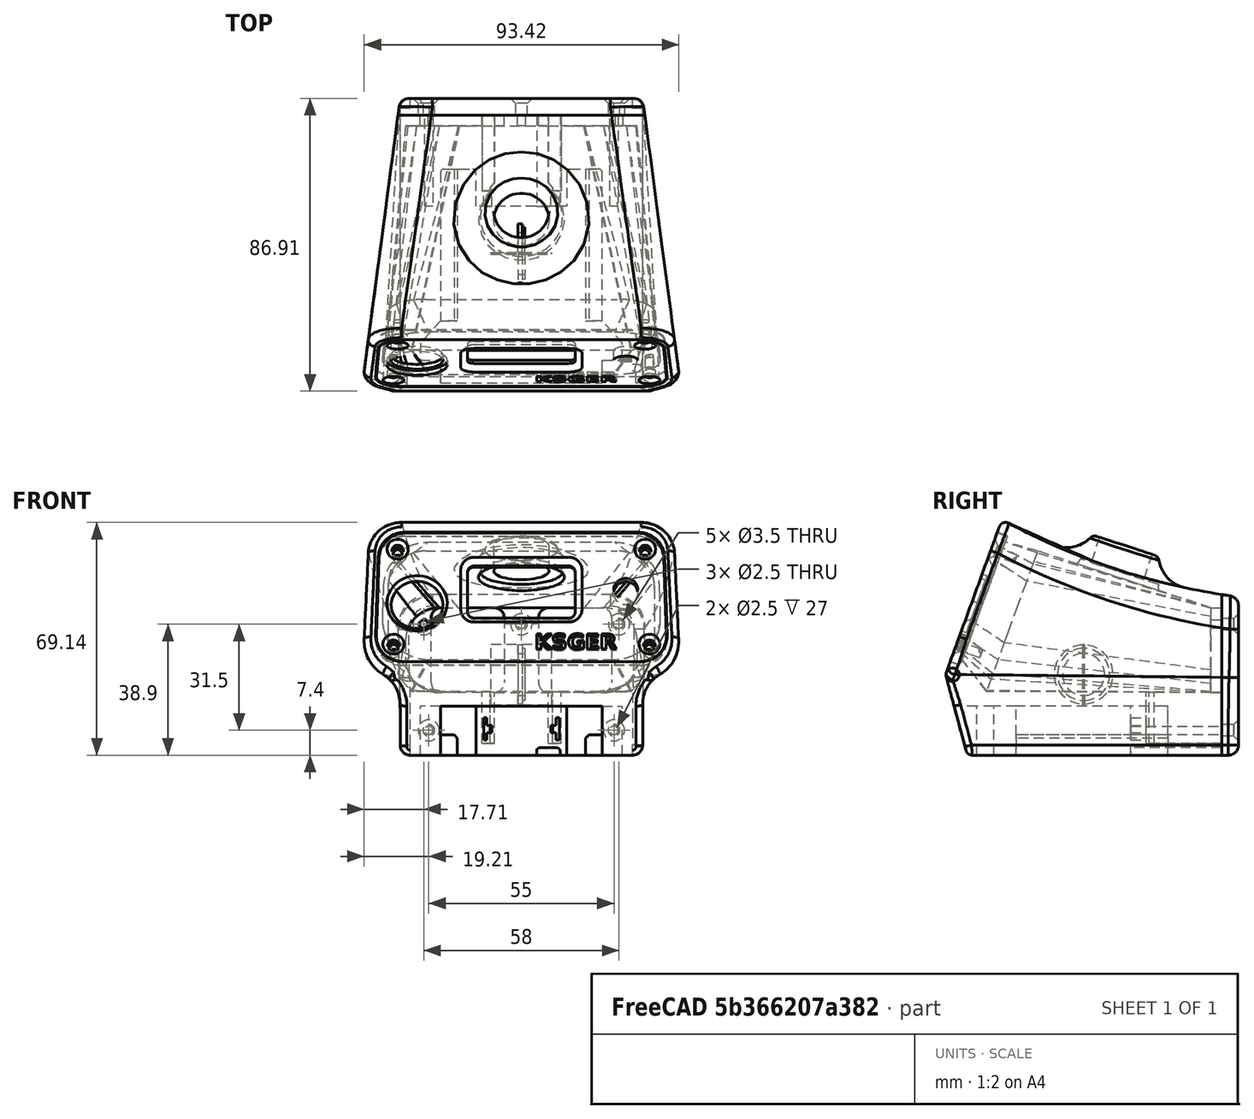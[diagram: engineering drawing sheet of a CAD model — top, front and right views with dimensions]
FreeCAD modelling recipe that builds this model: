
FCSTD DOCUMENT  (FreeCAD 0.20R29410 (Git))
Label: solder_station5c_snap
License: All rights reserved
LicenseURL: http://en.wikipedia.org/wiki/All_rights_reserved
objects: Sketcher::SketchObject×22, PartDesign::Pocket×12, PartDesign::Fillet×8, Part::FeaturePython×6, PartDesign::Body×5, Mesh::Feature×5, App::DocumentObjectGroup×4, PartDesign::FeatureBase×3, PartDesign::Chamfer×3, PartDesign::Pad×2, PartDesign::Revolution×2, Spreadsheet::Sheet×1, Part::Plane×1, Part::Loft×1, Part::Extrusion×1, Part::MultiCommon×1, Part::Box×1, PartDesign::SubtractiveLoft×1, PartDesign::Groove×1, PartDesign::Plane×1, +2 more types
note: 101 computed .brp shape members not serialized (recipe doc carries the construction recipe); baked Part::Feature solids carry a one-line shape summary decoded from their .brp

FEATURE [Sketcher::SketchObject] Sketch  label="RearSupport"
  AttachmentOffset = pos=(0,0,-37.8) rot=(0,0,1;0rad)
  FullyConstrained = true
  MapMode = 5
  Placement = pos=(0,37.8,8.4e-15) rot=(1,0,0;1.5708rad)
  Support = -> [XZ_Plane005]
  expr: .AttachmentOffset.Base.z = -<<param>>.mid_depth / 2 + <<param>>.wall
  expr: Constraints[24] = 3
  expr: Constraints[37] = <<param>>.bottom_height
  expr: Constraints[38] = <<param>>.floor
  expr: Constraints[39] = <<param>>.rear_height - <<param>>.wall
  expr: Constraints[47] = <<param>>.reart_screw_width2
  expr: Constraints[48] = <<param>>.rear_screw_width1
  expr: Constraints[49] = <<param>>.screw_hole
  expr: Constraints[50] = <<param>>.rear_screw_height
  expr: Constraints[51] = <<param>>.rear_screw_height
  expr: Constraints[52] = <<param>>.rear_screw_offset
  sketch-geometry (22):
    g0: LineSegment StartX=-23.8 StartY=19.8 StartZ=0 EndX=-8.1 EndY=19.8 EndZ=0
    g1: LineSegment StartX=26.8 StartY=16.8 StartZ=0 EndX=26.8 EndY=-2.4 EndZ=0
    g2: LineSegment StartX=23.8 StartY=-5.4 StartZ=0 EndX=8.1 EndY=-5.4 EndZ=0
    g3: LineSegment StartX=-26.8 StartY=-2.4 StartZ=0 EndX=-26.8 EndY=16.8 EndZ=0
    g4: LineSegment StartX=-5.1 StartY=16.8 StartZ=0 EndX=-5.1 EndY=-2.4 EndZ=0
    g5: LineSegment StartX=5.1 StartY=16.8 StartZ=0 EndX=5.1 EndY=-2.4 EndZ=0
    g6: LineSegment StartX=8.1 StartY=19.8 StartZ=0 EndX=23.8 EndY=19.8 EndZ=0
    g7: LineSegment StartX=-8.1 StartY=-5.4 StartZ=0 EndX=-23.8 EndY=-5.4 EndZ=0
    g8: ArcOfCircle CenterX=-8.1 CenterY=16.8 CenterZ=0 NormalX=0 NormalY=0 NormalZ=1 AngleXU=0 Radius=3 StartAngle=0 EndAngle=1.5708
    g9: ArcOfCircle CenterX=8.1 CenterY=16.8 CenterZ=0 NormalX=0 NormalY=0 NormalZ=1 AngleXU=0 Radius=3 StartAngle=1.5708 EndAngle=3.14159
    g10: ArcOfCircle CenterX=-8.1 CenterY=-2.4 CenterZ=0 NormalX=0 NormalY=0 NormalZ=1 AngleXU=0 Radius=3 StartAngle=4.71239 EndAngle=6.28319
    g11: ArcOfCircle CenterX=8.1 CenterY=-2.4 CenterZ=0 NormalX=0 NormalY=0 NormalZ=1 AngleXU=0 Radius=3 StartAngle=3.14159 EndAngle=4.71239
    g12: ArcOfCircle CenterX=-23.8 CenterY=16.8 CenterZ=0 NormalX=0 NormalY=0 NormalZ=1 AngleXU=0 Radius=3 StartAngle=1.5708 EndAngle=3.14159
    g13: ArcOfCircle CenterX=-23.8 CenterY=-2.4 CenterZ=0 NormalX=0 NormalY=0 NormalZ=1 AngleXU=0 Radius=3 StartAngle=3.14159 EndAngle=4.71239
    g14: ArcOfCircle CenterX=23.8 CenterY=16.8 CenterZ=0 NormalX=0 NormalY=0 NormalZ=1 AngleXU=0 Radius=3 StartAngle=3e-16 EndAngle=1.5708
    g15: ArcOfCircle CenterX=23.8 CenterY=-2.4 CenterZ=0 NormalX=0 NormalY=0 NormalZ=1 AngleXU=0 Radius=3 StartAngle=4.71239 EndAngle=6.28319
    g16: Circle CenterX=0 CenterY=-24 CenterZ=0 NormalX=0 NormalY=0 NormalZ=1 AngleXU=0 Radius=3
    g17: Circle CenterX=0 CenterY=14.9 CenterZ=0 NormalX=0 NormalY=0 NormalZ=1 AngleXU=0 Radius=1.25
    g18: Circle CenterX=-29 CenterY=14.9 CenterZ=0 NormalX=0 NormalY=0 NormalZ=1 AngleXU=0 Radius=1.25
    g19: Circle CenterX=-27.5 CenterY=-16.6 CenterZ=0 NormalX=0 NormalY=0 NormalZ=1 AngleXU=0 Radius=1.25
    g20: Circle CenterX=27.5 CenterY=-16.6 CenterZ=0 NormalX=0 NormalY=0 NormalZ=1 AngleXU=0 Radius=1.25
    g21: Circle CenterX=29 CenterY=14.9 CenterZ=0 NormalX=0 NormalY=0 NormalZ=1 AngleXU=0 Radius=1.25
  constraints (53):
    c: Horizontal(g0)
    c: Horizontal(g2)
    c: Vertical(g1)
    c: Vertical(g3)
    c: Vertical(g4)
    c: Vertical(g5)
    c: Tangent(g0,g6)
    c: Tangent(g2,g7)
    c: Tangent(g0,g8) = 1.5708
    c: Tangent(g4,g8) = 1.5708
    c: Tangent(g5,g9) = -1.5708
    c: Tangent(g6,g9) = 1.5708
    c: Tangent(g7,g10) = 1.5708
    c: Tangent(g4,g10) = 1.5708
    c: Tangent(g5,g11) = -1.5708
    c: Tangent(g2,g11) = 1.5708
    c: Tangent(g0,g12) = 1.5708
    c: Tangent(g3,g12) = 1.5708
    c: Tangent(g3,g13) = 1.5708
    c: Tangent(g7,g13) = 1.5708
    c: Tangent(g6,g14) = 1.5708
    c: Tangent(g1,g14) = 1.5708
    c: Tangent(g1,g15) = 1.5708
    c: Tangent(g2,g15) = 1.5708
    c: Radius(g9) = 3
    c: Equal(g12,g13)
    c: Equal(g13,g10)
    c: Equal(g10,g8)
    c: Equal(g11,g15)
    c: Equal(g15,g14)
    c: Equal(g14,g9)
    c: DistanceX(g4,g-1) = 5.1
    c: DistanceX(g5,g1) = 21.7
    c: Symmetric(g4,g5,g-2)
    c: Equal(g7,g2)
    c: PointOnObject(g16,g-2)
    c: Radius(g16) = 3
    c: DistanceY(g16,g-1) = 24
    c: DistanceY(g16,g2) = 18.6
    c: DistanceY(g16,g6) = 43.8
    c: PointOnObject(g17,g-2)
    c: Equal(g21,g18)
    c: Equal(g18,g19)
    c: Equal(g19,g20)
    c: Equal(g18,g17)
    c: Symmetric(g20,g19,g-2)
    c: Symmetric(g18,g21,g-2)
    c: DistanceX(g19,g20) = 55
    c: DistanceX(g18,g21) = 58
    c: Diameter(g19) = 2.5
    c: DistanceY(g20,g21) = 31.5
    c: DistanceY(g20,g17) = 31.5
    c: DistanceY(g16,g19) = 7.4
FEATURE [Spreadsheet::Sheet] Spreadsheet  label="param"
  cells = A1=Body; B2=top_depth; C2(top_depth)=70; B3=mid_depth; C3(mid_depth)=82; D3=half is rear reference; B4=bottom_depth; C4(bottom_depth)=75; B6=bottom_width; C6(bottom_width)=72; B7=bottom_height; C7(bottom_height)=24; B8=bottom_angle; C8(bottom_angle)=15; B10=rear_width; C10(rear_width)=72; B11=rear_height; C11(rear_height)=47; F11=41; B13=mid_width; C13(mid_width)=80; B14=mid_height; C14(mid_height)=56; F14=50; B16=front_width1; C16(front_width1)=92; D16=@top; E16=upper; F16=91; B17=front_width2; C17(front_width2)=95; D17=@mid; E17=lower; F17=94; B18=front_height; C18(front_height)=70; F18=64; B19=front_angle; C19(front_angle)=20; B21=wall; C21(wall)=3.2; B22=radius_big; C22(radius_big)=10; B23=radius_medium; C23(radius_medium)=3; B24=radius_small; C24(radius_small)=2; B25=arch; C25(arch)=200; A27=Button; B28=button_offset; C28(button_offset)=10; B29=button_inside_dia; C29(button_inside_dia)=20; B30=button_outside_dia; C30(button_outside_dia)=22; B31=button_height; C31(button_height)=30.6; F31=26; B32=button_extension; C32(button_extension)=8; B33=button_fillet; C33(button_fillet)=12; B34=button_angle; C34(button_angle)=-18; F34=-17; B35=button_hole; C35(button_hole)=16.4; B36=button_hole_center; C36(button_hole_center)=-0.5; A38=Battery Cuts; B39=batt_carveout; C39(batt_carveout)=14.6; B40=batt_rail; C40(batt_rail)=6; B41=batt_rail_length; C41(batt_rail_length)=45; A43=Terminals; B44=terminal_height; C44(terminal_height)=6.6; B45=terminal_thickness; C45(terminal_thickness)=1; B46=terminal_seperation; C46(terminal_seperation)=21.5; B47=terminal_offset; C47(terminal_offset)=4.5; B48=terminal_depth; C48(terminal_depth)=22.5; A50=Box Interior; B51=floor; C51(floor)=18.6; B52=rear_inside_width; C52(rear_inside_width)==C10 - C21; D52=calc; B53=rear_inside_height; C53(rear_inside_height)==C11 - C21; D53=calc; B54=mid_inside_width; C54(mid_inside_width)==C13; D54=calc; B55=mid_inside_height; C55(mid_inside_height)==C14 + 7; D55=calc; F55=6; B56=front_inside_width1; C56(front_inside_width1)==C63 - C59 * 2; D56=calc; E56=upper; B57=front_inside_width2; C57(front_inside_width2)==C64 - C59 * 2; D57=calc; E57=lower; B58=front_inside_height; C58(front_inside_height)==C65 - C60 * 2; D58=calc; B59=front_width_lip_width; C59(front_width_lip_width)=3; B60=front_inside_lip_height; C60(front_inside_lip_height)=2; A62=Face; B63=face_width1; C63(face_width1)==84 + 1; D63=Dimension of opening in case (upper); B64=face_width2; C64(face_width2)==85.5 + 1; D64=Dimension of opening in case (lower); B65=face_height; C65(face_height)=41; D65=Dimension of actual opening in case; F65=35; B66=face_fit; C66(face_fit)=0.4; D66=Reduction of face dimensions for clearance with case; B67=face_thickness; C67(face_thickness)=3; D67=Face thickness; B68=face_radius; C68(face_radius)=8; D68=Corner radius; B69=face_offset; C69(face_offset)=2.8; D69=Axis origin to bottom face (reference); F69=2.8; B70=face_knob_x; C70(face_knob_x)=31; D70=Vertical center line of face to center of knob; B71=face_knob_y; C71(face_knob_y)=22.7; D71=Bottom of face to center of knob; B72=face_knob_tab; C72(face_knob_tab)=n/a; D72=Center to center distance of rotary dial shaft to tab; B73=face_knob_hole; C73(face_knob_hole)=7.2; D73=Hole size fo shaft; B74=face_screen_x; C74(face_screen_x)=15; D74=Center of knob to right edge of screen; B75=face_screen_y; C75(face_screen_y)=n/a; D75=Bottom of face to center of screen; B76=face_screen_width; C76(face_screen_width)=32; D76=Width of screen opening; B77=face_screen_height; C77(face_screen_height)=16.5; D77=Height of screen opening; B78=face_screen_radius; C78(face_screen_radius)=2; D78=Radius of screen opening; B79=face_plug_x; C79(face_plug_x)=31; D79=Center line of face to center of plug; B80=face_plug_y; C80(face_plug_y)=18.7; D80=Bottom of face to center of plug; B81=face_plug_hole; C81(face_plug_hole)=15.5; D81=Hole size for plug body; A83=Screws; B84=screw_hole; C84(screw_hole)=2.5; B86=front_screw_width1; C86(front_screw_width1)=73.5; D86=upper; B87=front_screw_width2; C87(front_screw_width2)=76; D87=lower; B88=front_screw_height; C88(front_screw_height)=30; F88=24; B89=front_screw_offset; C89(front_screw_offset)=5.5; B91=rear_screw_width1; C91(rear_screw_width1)=58; B92=reart_screw_width2; C92(reart_screw_width2)=55; B93=rear_screw_height; C93(rear_screw_height)=31.5; F93=25.5; +5 more cells
FEATURE [Sketcher::SketchObject] Sketch008  label="SketchButtonHole"
  AttachmentOffset = pos=(0,-0.5,30.6) rot=(1,0,0;-0.314159rad)
  FullyConstrained = true
  MapMode = 5
  Placement = pos=(0,-0.5,30.6) rot=(1,0,0;5.96903rad)
  Support = -> [XY_Plane005]
  expr: .AttachmentOffset.Base.y = <<param>>.button_hole_center
  expr: .AttachmentOffset.Base.z = <<param>>.button_height
  expr: .AttachmentOffset.Rotation.Angle = <<param>>.button_angle
  expr: Constraints[0] = <<param>>.button_hole
  expr: Constraints[2] = <<param>>.button_offset
  sketch-geometry (1):
    g0: Circle CenterX=0 CenterY=10 CenterZ=0 NormalX=0 NormalY=0 NormalZ=1 AngleXU=0 Radius=8.2
  constraints (3):
    c: Diameter(g0) = 16.4
    c: PointOnObject(g0,g-2)
    c: DistanceY(g-1,g0) = 10
FEATURE [Sketcher::SketchObject] Sketch012  label="SketchSide"
  AttachmentOffset = pos=(2.5,0,0) rot=(0,0,1;0rad)
  FullyConstrained = true
  MapMode = 5
  Placement = pos=(6e-16,2.5,-6e-16) rot=(0.57735,0.57735,0.57735;2.0944rad)
  Support = -> [YZ_Plane006]
  expr: .AttachmentOffset.Base.x = <<param>>.back_thickness / 2
  expr: Constraints[10] = <<param>>.bottom_height
  expr: Constraints[11] = 90 - <<param>>.bottom_angle
  expr: Constraints[12] = 90 - <<param>>.front_angle
  expr: Constraints[16] = <<param>>.front_height
  expr: Constraints[4] = <<param>>.rear_height - <<param>>.bottom_height
  expr: Constraints[5] = <<param>>.arch
  expr: Constraints[6] = <<param>>.mid_depth + <<param>>.back_thickness
  sketch-geometry (6):
    g0: LineSegment StartX=43.5 StartY=0 StartZ=0 EndX=43.5 EndY=23 EndZ=0
    g1: LineSegment StartX=-43.5 StartY=0 StartZ=0 EndX=-26.7574 EndY=46 EndZ=0
    g2: ArcOfCircle CenterX=69.5235 CenterY=221.3 CenterZ=0 NormalX=0 NormalY=0 NormalZ=1 AngleXU=0 Radius=200 StartAngle=4.21013 EndAngle=4.5819
    g3: LineSegment StartX=-43.5 StartY=0 StartZ=0 EndX=-37.0692 EndY=-24 EndZ=0
    g4: LineSegment StartX=-37.0692 StartY=-24 StartZ=0 EndX=43.5 EndY=-24 EndZ=0
    g5: LineSegment StartX=43.5 StartY=-24 StartZ=0 EndX=43.5 EndY=0 EndZ=0
  constraints (18):
    c: PointOnObject(g1,g-1)
    c: Vertical(g0)
    c: Coincident(g2,g0)
    c: Symmetric(g1,g0,g-2)
    c: DistanceY(g0,g0) = 23
    c: Radius(g2) = 200
    c: DistanceX(g1,g0) = 87
    c: Horizontal(g4)
    c: Coincident(g5,g4)
    c: Vertical(g5)
    c: DistanceY(g4,g-1) = 24
    c: Angle(g3,g-1) = 1.309
    c: Angle(g-1,g1) = 1.22173
    c: Coincident(g3,g1)
    c: Coincident(g5,g0)
    c: Coincident(g2,g1)
    c: DistanceY(g4,g1) = 70
    c: Coincident(g3,g4)
FEATURE [Sketcher::SketchObject] Sketch018  label="SketchBat1"
  AttachmentOffset = pos=(0,0,-24) rot=(0,0,1;0rad)
  FullyConstrained = true
  MapMode = 5
  Placement = pos=(0,0,-24) rot=(0,0,1;0rad)
  Support = -> [XY_Plane005]
  expr: .AttachmentOffset.Base.z = -<<param>>.bottom_height
  expr: Constraints[63] = <<param>>.batt_rail_length
  expr: Constraints[64] = <<param>>.mid_depth / 2
  sketch-geometry (21):
    g0: LineSegment StartX=-24 StartY=-41.7082 StartZ=0 EndX=24 EndY=-41.7082 EndZ=0
    g1: LineSegment StartX=24 StartY=-41.7082 StartZ=0 EndX=24 EndY=-31.7082 EndZ=0
    g2: LineSegment StartX=24 StartY=-31.7082 StartZ=0 EndX=30 EndY=-31.7082 EndZ=0
    g3: LineSegment StartX=30 StartY=-31.7082 StartZ=0 EndX=30 EndY=-26.7082 EndZ=0
    g4: LineSegment StartX=30 StartY=-26.7082 StartZ=0 EndX=24 EndY=-20 EndZ=0
    g5: LineSegment StartX=24 StartY=-20 StartZ=0 EndX=24 EndY=24 EndZ=0
    g6: LineSegment StartX=13.5 StartY=24 StartZ=0 EndX=13.5 EndY=14 EndZ=0
    g7: LineSegment StartX=13.5 StartY=14 StartZ=0 EndX=-13.5 EndY=14 EndZ=0
    g8: LineSegment StartX=-13.5 StartY=14 StartZ=0 EndX=-13.5 EndY=24 EndZ=0
    g9: LineSegment StartX=-24 StartY=24 StartZ=0 EndX=-24 EndY=-20 EndZ=0
    g10: LineSegment StartX=-24 StartY=-20 StartZ=0 EndX=-30 EndY=-26.7082 EndZ=0
    g11: LineSegment StartX=-30 StartY=-26.7082 StartZ=0 EndX=-30 EndY=-31.7082 EndZ=0
    g12: LineSegment StartX=-30 StartY=-31.7082 StartZ=0 EndX=-24 EndY=-31.7082 EndZ=0
    g13: LineSegment StartX=-24 StartY=-31.7082 StartZ=0 EndX=-24 EndY=-41.7082 EndZ=0
    g14: Circle CenterX=0 CenterY=41 CenterZ=0 NormalX=0 NormalY=0 NormalZ=1 AngleXU=0 Radius=4
    g15: ArcOfCircle CenterX=-14.5 CenterY=24 CenterZ=0 NormalX=0 NormalY=0 NormalZ=1 AngleXU=0 Radius=1 StartAngle=6.28318 EndAngle=7.85399
    g16: LineSegment StartX=-23 StartY=25 StartZ=0 EndX=-14.5 EndY=25 EndZ=0
    g17: LineSegment StartX=14.5 StartY=25 StartZ=0 EndX=23 EndY=25 EndZ=0
    g18: ArcOfCircle CenterX=-23 CenterY=24 CenterZ=0 NormalX=0 NormalY=0 NormalZ=1 AngleXU=0 Radius=1 StartAngle=1.57079 EndAngle=3.1416
    g19: ArcOfCircle CenterX=14.5 CenterY=24 CenterZ=0 NormalX=0 NormalY=0 NormalZ=1 AngleXU=0 Radius=1 StartAngle=1.5708 EndAngle=3.14159
    g20: ArcOfCircle CenterX=23 CenterY=24 CenterZ=0 NormalX=0 NormalY=0 NormalZ=1 AngleXU=0 Radius=1.00001 StartAngle=2.75124e-06 EndAngle=1.5708
  constraints (65):
    c: Horizontal(g0)
    c: Coincident(g1,g0)
    c: Vertical(g1)
    c: Coincident(g2,g1)
    c: Horizontal(g2)
    c: Coincident(g3,g2)
    c: Coincident(g3,g4)
    c: Vertical(g5)
    c: Coincident(g6,g7)
    c: Coincident(g7,g8)
    c: Vertical(g8)
    c: Vertical(g9)
    c: Coincident(g10,g11)
    c: Vertical(g11)
    c: Coincident(g11,g12)
    c: Horizontal(g12)
    c: Coincident(g12,g13)
    c: Equal(g6,g8)
    c: Equal(g5,g9)
    c: Equal(g4,g10)
    c: Equal(g3,g11)
    c: Equal(g12,g2)
    c: Equal(g1,g13)
    c: Coincident(g13,g0)
    c: Vertical(g13)
    c: DistanceX(g7,g7) = 27
    c: Symmetric(g7,g6,g-2)
    c: Distance(g4) = 9
    c: Vertical(g3)
    c: DistanceY(g3,g3) = 5
    c: DistanceX(g2,g2) = 6
    c: DistanceY(g1,g1) = 10
    c: DistanceX(g0,g0) = 48
    c: PointOnObject(g14,g-2)
    c: Coincident(g9,g10)
    c: Coincident(g5,g4)
    c: Coincident(g15,g8)
    c: Coincident(g16,g15)
    c: Tangent(g15,g8)
    c: Horizontal(g16)
    c: Horizontal(g17)
    c: DistanceX(g9,g5) = 48
    c: Symmetric(g4,g9,g-2)
    c: Equal(g16,g17)
    c: Coincident(g18,g9)
    c: Coincident(g18,g16)
    c: Equal(g18,g15)
    c: Tangent(g18,g16)
    c: Tangent(g18,g9)
    c: DistanceY(g6,g17) = 11
    c: Vertical(g6)
    c: Coincident(g19,g6)
    c: Coincident(g19,g17)
    c: Coincident(g20,g17)
    c: Coincident(g20,g5)
    c: Tangent(g20,g17)
    c: Tangent(g20,g5)
    c: Tangent(g19,g6)
    c: Tangent(g19,g17)
    c: Equal(g15,g19)
    c: Radius(g19) = 1
    c: Radius(g14) = 4
    c: DistanceY(g15,g14) = 16
    c: DistanceY(g9,g16) = 45
    c: DistanceY(g-1,g14) = 41
FEATURE [Sketcher::SketchObject] Sketch019  label="SketchBat2"
  AttachmentOffset = pos=(0,0,-25) rot=(0,0,1;0rad)
  FullyConstrained = true
  MapMode = 5
  Placement = pos=(0,25,5.6e-15) rot=(1,0,0;1.5708rad)
  Support = -> [XZ_Plane005]
  expr: .AttachmentOffset.Base.z = -<<param>>.mid_depth / 2 + 16
  expr: Constraints[17] = <<param>>.bottom_height
  expr: Constraints[18] = <<param>>.batt_rail
  expr: Constraints[19] = 48.01mm
  sketch-geometry (10):
    g0: LineSegment StartX=-24.005 StartY=-18 StartZ=0 EndX=-20.005 EndY=-18 EndZ=0
    g1: LineSegment StartX=-19.005 StartY=-24 StartZ=0 EndX=-24.005 EndY=-24 EndZ=0
    g2: LineSegment StartX=-24.005 StartY=-24 StartZ=0 EndX=-24.005 EndY=-18 EndZ=0
    g3: LineSegment StartX=24.005 StartY=-18 StartZ=0 EndX=20.005 EndY=-18 EndZ=0
    g4: LineSegment StartX=19.005 StartY=-24 StartZ=0 EndX=24.005 EndY=-24 EndZ=0
    g5: LineSegment StartX=24.005 StartY=-24 StartZ=0 EndX=24.005 EndY=-18 EndZ=0
    g6: LineSegment StartX=-19.005 StartY=-19 StartZ=0 EndX=-19.005 EndY=-24 EndZ=0
    g7: LineSegment StartX=19.005 StartY=-24 StartZ=0 EndX=19.005 EndY=-19 EndZ=0
    g8: LineSegment StartX=-20.005 StartY=-18 StartZ=0 EndX=-19.005 EndY=-19 EndZ=0
    g9: LineSegment StartX=19.005 StartY=-19 StartZ=0 EndX=20.005 EndY=-18 EndZ=0
  constraints (29):
    c: Coincident(g1,g2)
    c: Coincident(g2,g0)
    c: Horizontal(g0)
    c: Horizontal(g1)
    c: Vertical(g2)
    c: Coincident(g4,g5)
    c: Coincident(g5,g3)
    c: Horizontal(g3)
    c: Horizontal(g4)
    c: Vertical(g5)
    c: Coincident(g6,g1)
    c: Vertical(g6)
    c: Equal(g1,g4)
    c: Coincident(g7,g4)
    c: Vertical(g7)
    c: Equal(g6,g7)
    c: Symmetric(g1,g4,g-2)
    c: DistanceY(g1,g-1) = 24
    c: DistanceY(g4,g3) = 6
    c: DistanceX(g1,g4) = 48.01
    c: DistanceX(g4,g4) = 5
    c: Coincident(g8,g0)
    c: Coincident(g8,g6)
    c: Coincident(g9,g7)
    c: Coincident(g9,g3)
    c: Equal(g0,g3)
    c: Equal(g2,g5)
    c: DistanceX(g0,g0) = 4
    c: DistanceY(g1,g6) = 5
FEATURE [Sketcher::SketchObject] Sketch021  label="SketchButton"
  AttachmentOffset = pos=(10,30.6,0) rot=(0,0,1;-0.314159rad)
  FullyConstrained = true
  MapMode = 5
  Placement = pos=(-4.6e-15,10,30.6) rot=(-0.506732,-0.697457,-0.506732;4.35963rad)
  Support = -> [YZ_Plane005]
  expr: .AttachmentOffset.Base.x = <<param>>.button_offset
  expr: .AttachmentOffset.Base.y = <<param>>.button_height
  expr: .AttachmentOffset.Rotation.Angle = <<param>>.button_angle
  expr: Constraints[6] = <<param>>.button_extension
  expr: Constraints[7] = <<param>>.button_outside_dia / 2
  sketch-geometry (5):
    g0: LineSegment StartX=0 StartY=0 StartZ=0 EndX=0 EndY=8 EndZ=0
    g1: LineSegment StartX=0 StartY=8 StartZ=0 EndX=9 EndY=8 EndZ=0
    g2: LineSegment StartX=0 StartY=0 StartZ=0 EndX=11 EndY=0 EndZ=0
    g3: LineSegment StartX=11 StartY=0 StartZ=0 EndX=11 EndY=6 EndZ=0
    g4: ArcOfCircle CenterX=9 CenterY=6 CenterZ=0 NormalX=0 NormalY=0 NormalZ=1 AngleXU=0 Radius=2 StartAngle=1e-16 EndAngle=1.5708
  constraints (13):
    c: Coincident(g0,g-1)
    c: PointOnObject(g0,g-2)
    c: Coincident(g1,g0)
    c: Horizontal(g1)
    c: Coincident(g2,g0)
    c: Horizontal(g2)
    c: DistanceY(g0,g0) = 8
    c: DistanceX(g2,g2) = 11
    c: Coincident(g3,g2)
    c: Vertical(g3)
    c: Radius(g4) = 2
    c: Tangent(g4,g1) = 1.5708
    c: Tangent(g4,g3) = -1.5708
FEATURE [Sketcher::SketchObject] Sketch022  label="SketchRearInside"
  AttachmentOffset = pos=(0,0,-37.8) rot=(0,0,1;0rad)
  FullyConstrained = true
  MapMode = 5
  Placement = pos=(0,37.8,8.4e-15) rot=(1,0,0;1.5708rad)
  Support = -> [XZ_Plane005]
  expr: .AttachmentOffset.Base.z = -<<param>>.mid_depth / 2 + <<param>>.wall
  expr: Constraints[12] = <<param>>.radius_big
  expr: Constraints[18] = <<param>>.rear_inside_width
  expr: Constraints[26] = <<param>>.bottom_height
  expr: Constraints[27] = <<param>>.rear_inside_height
  expr: Constraints[29] = <<param>>.floor
  sketch-geometry (9):
    g0: LineSegment StartX=-34.4 StartY=9.80002 StartZ=0 EndX=-34.4 EndY=4.59998 EndZ=0
    g1: LineSegment StartX=-24.4 StartY=-5.4 StartZ=0 EndX=24.4 EndY=-5.4 EndZ=0
    g2: LineSegment StartX=34.4 StartY=4.59998 StartZ=0 EndX=34.4 EndY=9.80002 EndZ=0
    g3: LineSegment StartX=-24.4 StartY=19.8 StartZ=0 EndX=24.4 EndY=19.8 EndZ=0
    g4: ArcOfCircle CenterX=24.4 CenterY=9.8 CenterZ=0 NormalX=0 NormalY=0 NormalZ=1 AngleXU=0 Radius=10 StartAngle=1.745e-06 EndAngle=1.57079
    g5: ArcOfCircle CenterX=24.4 CenterY=4.6 CenterZ=0 NormalX=0 NormalY=0 NormalZ=1 AngleXU=0 Radius=10 StartAngle=4.71239 EndAngle=6.28318
    g6: ArcOfCircle CenterX=-24.4 CenterY=9.8 CenterZ=0 NormalX=0 NormalY=0 NormalZ=1 AngleXU=0 Radius=10 StartAngle=1.5708 EndAngle=3.14159
    g7: ArcOfCircle CenterX=-24.4 CenterY=4.6 CenterZ=0 NormalX=0 NormalY=0 NormalZ=1 AngleXU=0 Radius=10 StartAngle=3.14159 EndAngle=4.71239
    g8: Circle CenterX=0 CenterY=-24 CenterZ=0 NormalX=0 NormalY=0 NormalZ=1 AngleXU=0 Radius=3
  constraints (30):
    c: Vertical(g0)
    c: Horizontal(g1)
    c: Vertical(g2)
    c: Horizontal(g3)
    c: Equal(g3,g1)
    c: Equal(g0,g2)
    c: Coincident(g4,g3)
    c: Coincident(g4,g2)
    c: Coincident(g5,g2)
    c: Coincident(g5,g1)
    c: Coincident(g6,g0)
    c: Coincident(g6,g3)
    c: Radius(g6) = 10
    c: Equal(g6,g4)
    c: Equal(g4,g5)
    c: Coincident(g7,g1)
    c: Coincident(g7,g0)
    c: Equal(g5,g7)
    c: DistanceX(g0,g2) = 68.8
    c: Symmetric(g0,g2,g-2)
    c: Tangent(g4,g2)
    c: Tangent(g4,g3)
    c: Tangent(g5,g2)
    c: Tangent(g5,g1)
    c: Tangent(g6,g3)
    c: PointOnObject(g8,g-2)
    c: DistanceY(g8,g-1) = 24
    c: DistanceY(g8,g3) = 43.8
    c: Radius(g8) = 3
    c: DistanceY(g8,g1) = 18.6
FEATURE [Sketcher::SketchObject] Sketch024  label="SketchFaceCut"
  AttachmentOffset = pos=(0,0,37.6) rot=(1,0,0;-0.349066rad)
  FullyConstrained = true
  MapMode = 5
  Placement = pos=(0,-37.6,-8.3e-15) rot=(-1,0,0;5.06145rad)
  Support = -> [XZ_Plane005]
  expr: .AttachmentOffset.Base.z = <<param>>.mid_depth / 2 - <<param>>.face_thickness - 0.4
  expr: .AttachmentOffset.Rotation.Angle = -<<param>>.front_angle
  expr: Constraints[13] = <<param>>.face_radius
  expr: Constraints[22] = <<param>>.face_width1
  expr: Constraints[23] = <<param>>.face_width2
  expr: Constraints[24] = <<param>>.face_offset
  expr: Constraints[25] = <<param>>.face_height
  sketch-geometry (8):
    g0: LineSegment StartX=-34.5036 StartY=43.8 StartZ=0 EndX=34.5036 EndY=43.8 EndZ=0
    g1: LineSegment StartX=42.5 StartY=36.0399 StartZ=0 EndX=43.25 EndY=11.0399 EndZ=0
    g2: LineSegment StartX=35.2536 StartY=2.8 StartZ=0 EndX=-35.2536 EndY=2.8 EndZ=0
    g3: LineSegment StartX=-43.25 StartY=11.0399 StartZ=0 EndX=-42.5 EndY=36.0399 EndZ=0
    g4: ArcOfCircle CenterX=34.5036 CenterY=35.8 CenterZ=0 NormalX=0 NormalY=0 NormalZ=1 AngleXU=0 Radius=8 StartAngle=0.0299892 EndAngle=1.5708
    g5: ArcOfCircle CenterX=35.2536 CenterY=10.8 CenterZ=0 NormalX=0 NormalY=0 NormalZ=1 AngleXU=0 Radius=8 StartAngle=4.71239 EndAngle=6.31318
    g6: ArcOfCircle CenterX=-34.5036 CenterY=35.8 CenterZ=0 NormalX=0 NormalY=0 NormalZ=1 AngleXU=0 Radius=8 StartAngle=1.5708 EndAngle=3.1116
    g7: ArcOfCircle CenterX=-35.2536 CenterY=10.8 CenterZ=0 NormalX=0 NormalY=0 NormalZ=1 AngleXU=0 Radius=8 StartAngle=3.1116 EndAngle=4.71239
  constraints (27):
    c: Horizontal(g0)
    c: Coincident(g4,g0)
    c: Coincident(g4,g1)
    c: Coincident(g5,g1)
    c: Coincident(g5,g2)
    c: Coincident(g6,g0)
    c: Coincident(g6,g3)
    c: Coincident(g7,g3)
    c: Coincident(g7,g2)
    c: Equal(g1,g3)
    c: Equal(g4,g6)
    c: Equal(g6,g7)
    c: Equal(g7,g5)
    c: Radius(g4) = 8
    c: Tangent(g6,g3)
    c: Tangent(g7,g3)
    c: Tangent(g7,g2)
    c: Tangent(g6,g0)
    c: Tangent(g4,g0)
    c: Tangent(g4,g1)
    c: Tangent(g5,g1)
    c: Tangent(g5,g2)
    c: DistanceX(g3,g1) = 85
    c: DistanceX(g3,g1) = 86.5
    c: DistanceY(g-1,g2) = 2.8
    c: DistanceY(g2,g0) = 41
    c: Symmetric(g2,g2,g-2)
FEATURE [Sketcher::SketchObject] Sketch025  label="SketchMidInside"
  AttachmentOffset = pos=(0,0,27) rot=(1,0,0;-0.349066rad)
  FullyConstrained = true
  MapMode = 5
  Placement = pos=(0,-27,-6e-15) rot=(-1,0,0;5.06145rad)
  Support = -> [XZ_Plane005]
  expr: .AttachmentOffset.Base.z = <<param>>.mid_depth / 2 - 14
  expr: .AttachmentOffset.Rotation.Angle = -<<param>>.front_angle
  expr: Constraints[10] = <<param>>.radius_big + 1
  expr: Constraints[11] = <<param>>.floor
  expr: Constraints[12] = Spreadsheet.mid_inside_width - 1
  expr: Constraints[14] = <<param>>.mid_inside_height
  expr: Constraints[23] = <<param>>.mid_width - 15
  expr: Constraints[4] = <<param>>.bottom_height
  sketch-geometry (9):
    g0: LineSegment StartX=-28.5 StartY=39 StartZ=0 EndX=28.5 EndY=39 EndZ=0
    g1: LineSegment StartX=39.5 StartY=28 StartZ=0 EndX=39.5 EndY=10 EndZ=0
    g2: LineSegment StartX=32.5 StartY=-5.4 StartZ=0 EndX=-32.5 EndY=-5.4 EndZ=0
    g3: LineSegment StartX=-39.5 StartY=10 StartZ=0 EndX=-39.5 EndY=28 EndZ=0
    g4: Circle CenterX=0 CenterY=-24 CenterZ=0 NormalX=0 NormalY=0 NormalZ=1 AngleXU=0 Radius=3
    g5: ArcOfCircle CenterX=-28.5 CenterY=28 CenterZ=0 NormalX=0 NormalY=0 NormalZ=1 AngleXU=0 Radius=11 StartAngle=1.5708 EndAngle=3.14159
    g6: ArcOfCircle CenterX=28.5 CenterY=28 CenterZ=0 NormalX=0 NormalY=0 NormalZ=1 AngleXU=0 Radius=11 StartAngle=0 EndAngle=1.5708
    g7: ArcOfCircle CenterX=-15.553 CenterY=11.5941 CenterZ=0 NormalX=0 NormalY=0 NormalZ=1 AngleXU=0 Radius=24 StartAngle=3.20806 EndAngle=3.92838
    g8: ArcOfCircle CenterX=15.553 CenterY=11.5941 CenterZ=0 NormalX=0 NormalY=0 NormalZ=1 AngleXU=0 Radius=24 StartAngle=5.4964 EndAngle=6.21672
  constraints (25):
    c: Vertical(g1)
    c: Vertical(g3)
    c: PointOnObject(g4,g-2)
    c: Radius(g4) = 3
    c: DistanceY(g4,g-1) = 24
    c: Tangent(g3,g5) = 1.5708
    c: Tangent(g0,g5) = 1.5708
    c: Tangent(g0,g6) = 1.5708
    c: Tangent(g1,g6) = 1.5708
    c: Equal(g6,g5)
    c: Radius(g6) = 11
    c: DistanceY(g4,g2) = 18.6
    c: DistanceX(g3,g1) = 79
    c: Symmetric(g2,g2,g-2)
    c: DistanceY(g4,g0) = 63
    c: Symmetric(g0,g0,g-2)
    c: Equal(g3,g1)
    c: Coincident(g7,g2)
    c: Coincident(g8,g1)
    c: Coincident(g8,g2)
    c: Coincident(g7,g3)
    c: Equal(g8,g7)
    c: Radius(g8) = 24
    c: DistanceX(g2,g2) = 65
    c: DistanceY(g1,g1) = 18
FEATURE [Sketcher::SketchObject] Sketch026  label="SketchFrontScrews"
  AttachmentOffset = pos=(0,0,38) rot=(1,0,0;-0.349066rad)
  FullyConstrained = true
  MapMode = 5
  Placement = pos=(0,-38,-8.4e-15) rot=(-1,0,0;5.06145rad)
  Support = -> [XZ_Plane005]
  expr: .AttachmentOffset.Base.z = <<param>>.mid_depth / 2 - <<param>>.face_thickness
  expr: .AttachmentOffset.Rotation.Angle = -<<param>>.front_angle
  expr: Constraints[0] = <<param>>.front_screw_width1
  expr: Constraints[13] = <<param>>.screw_hole
  expr: Constraints[1] = <<param>>.front_screw_width2
  expr: Constraints[2] = <<param>>.front_screw_height
  expr: Constraints[9] = <<param>>.face_offset + <<param>>.front_screw_offset
  sketch-geometry (6):
    g0: Circle CenterX=-36.75 CenterY=38.3 CenterZ=0 NormalX=0 NormalY=0 NormalZ=1 AngleXU=0 Radius=1.25
    g1: Circle CenterX=36.75 CenterY=38.3 CenterZ=0 NormalX=0 NormalY=0 NormalZ=1 AngleXU=0 Radius=1.25
    g2: Circle CenterX=-38 CenterY=8.3 CenterZ=0 NormalX=0 NormalY=0 NormalZ=1 AngleXU=0 Radius=1.25
    g3: Circle CenterX=38 CenterY=8.3 CenterZ=0 NormalX=0 NormalY=0 NormalZ=1 AngleXU=0 Radius=1.25
    g4: LineSegment StartX=-36.75 StartY=38.3 StartZ=0 EndX=36.75 EndY=38.3 EndZ=0
    g5: LineSegment StartX=-38 StartY=8.3 StartZ=0 EndX=38 EndY=8.3 EndZ=0
  constraints (14):
    c: DistanceX(g0,g1) = 73.5
    c: DistanceX(g2,g3) = 76
    c: DistanceY(g3,g1) = 30
    c: Coincident(g4,g0)
    c: Coincident(g4,g1)
    c: Coincident(g5,g2)
    c: Coincident(g5,g3)
    c: Symmetric(g2,g3,g-2)
    c: Symmetric(g0,g1,g-2)
    c: DistanceY(g-1,g3) = 8.3
    c: Equal(g0,g2)
    c: Equal(g2,g3)
    c: Equal(g3,g1)
    c: Diameter(g0) = 2.5
FEATURE [Sketcher::SketchObject] Sketch023  label="SketchFrontInside"
  AttachmentOffset = pos=(0,0,38) rot=(1,0,0;-0.349066rad)
  ExternalGeometry = -> [Sketch026,Sketch024]
  FullyConstrained = true
  MapMode = 5
  Placement = pos=(0,-38,-8.4e-15) rot=(-1,0,0;5.06145rad)
  Support = -> [XZ_Plane005]
  expr: .AttachmentOffset.Base.z = <<param>>.mid_depth / 2 - <<param>>.face_thickness
  expr: .AttachmentOffset.Rotation.Angle = -<<param>>.front_angle
  sketch-geometry (16):
    g0: LineSegment StartX=-27.5 StartY=4.93681 StartZ=0 EndX=27.5 EndY=4.93681 EndZ=0
    g1: LineSegment StartX=27.5 StartY=41.9368 StartZ=0 EndX=-27.5 EndY=41.9368 EndZ=0
    g2: LineSegment StartX=-40.95 StartY=28 StartZ=0 EndX=-41.25 EndY=18 EndZ=0
    g3: LineSegment StartX=40.95 StartY=28 StartZ=0 EndX=41.25 EndY=18 EndZ=0
    g4: ArcOfCircle CenterX=36.75 CenterY=38.3 CenterZ=0 NormalX=0 NormalY=0 NormalZ=1 AngleXU=0 Radius=3 StartAngle=2.46996 EndAngle=5.23356
    g5: ArcOfCircle CenterX=27.5 CenterY=27.5965 CenterZ=0 NormalX=0 NormalY=0 NormalZ=1 AngleXU=0 Radius=13.4561 StartAngle=0.02999 EndAngle=0.646118
    g6: ArcOfCircle CenterX=27.5 CenterY=27.5965 CenterZ=0 NormalX=0 NormalY=0 NormalZ=1 AngleXU=0 Radius=14.3403 StartAngle=1.06869 EndAngle=1.5708
    g7: ArcOfCircle CenterX=38 CenterY=8.3 CenterZ=0 NormalX=0 NormalY=0 NormalZ=1 AngleXU=0 Radius=3 StartAngle=1.04132 EndAngle=3.41706
    g8: ArcOfCircle CenterX=27.5 CenterY=17.5875 CenterZ=0 NormalX=0 NormalY=0 NormalZ=1 AngleXU=0 Radius=13.7562 StartAngle=5.77461 EndAngle=6.31318
    g9: ArcOfCircle CenterX=27.5 CenterY=17.5875 CenterZ=0 NormalX=0 NormalY=0 NormalZ=1 AngleXU=0 Radius=12.6507 StartAngle=4.71239 EndAngle=5.35813
    g10: ArcOfCircle CenterX=-36.75 CenterY=38.3 CenterZ=0 NormalX=0 NormalY=0 NormalZ=1 AngleXU=0 Radius=3 StartAngle=4.19123 EndAngle=6.95482
    g11: ArcOfCircle CenterX=-27.5 CenterY=27.5965 CenterZ=0 NormalX=0 NormalY=0 NormalZ=1 AngleXU=0 Radius=13.456 StartAngle=2.49547 EndAngle=3.1116
    g12: ArcOfCircle CenterX=-27.5 CenterY=27.5965 CenterZ=0 NormalX=0 NormalY=0 NormalZ=1 AngleXU=0 Radius=14.3403 StartAngle=1.5708 EndAngle=2.0729
    g13: ArcOfCircle CenterX=-38 CenterY=8.3 CenterZ=0 NormalX=0 NormalY=0 NormalZ=1 AngleXU=0 Radius=3 StartAngle=6.00772 EndAngle=8.38345
    g14: ArcOfCircle CenterX=-27.5 CenterY=17.5875 CenterZ=0 NormalX=0 NormalY=0 NormalZ=1 AngleXU=0 Radius=13.7562 StartAngle=3.1116 EndAngle=3.65016
    g15: ArcOfCircle CenterX=-27.5 CenterY=17.5875 CenterZ=0 NormalX=0 NormalY=0 NormalZ=1 AngleXU=0 Radius=12.6507 StartAngle=4.06664 EndAngle=4.71239
  constraints (42):
    c: Symmetric(g0,g0,g-2)
    c: Symmetric(g1,g1,g-2)
    c: DistanceY(g3,g3) = 10
    c: Equal(g3,g2)
    c: Equal(g1,g0)
    c: DistanceX(g1,g1) = 55
    c: Coincident(g4,g-3)
    c: Coincident(g5,g4)
    c: Coincident(g6,g4)
    c: Radius(g4) = 3
    c: Tangent(g5,g3) = 1.5708
    c: Parallel(g3,g-8)
    c: Tangent(g6,g1) = -1.5708
    c: DistanceX(g3,g-8) = 2
    c: Parallel(g-7,g2)
    c: DistanceX(g-7,g2) = 2
    c: Coincident(g7,g-4)
    c: Coincident(g8,g7)
    c: Coincident(g9,g7)
    c: Tangent(g8,g3) = 1.5708
    c: Tangent(g9,g0) = -1.5708
    c: Coincident(g9,g8)
    c: Coincident(g5,g6)
    c: DistanceY(g-10,g0) = 2
    c: DistanceY(g1,g-9) = 2
    c: Coincident(g10,g-6)
    c: Coincident(g11,g10)
    c: Coincident(g12,g10)
    c: Coincident(g13,g-5)
    c: Coincident(g14,g13)
    c: Coincident(g15,g13)
    c: Tangent(g12,g1) = -1.5708
    c: Tangent(g11,g2) = -1.5708
    c: Coincident(g11,g12)
    c: Coincident(g14,g15)
    c: Tangent(g14,g2) = -1.5708
    c: Tangent(g15,g0) = -1.5708
    c: Equal(g10,g13)
    c: Equal(g13,g7)
    c: Equal(g7,g4)
    c: Equal(g12,g6)
    c: DistanceY(g-1,g3) = 18
FEATURE [Sketcher::SketchObject] Sketch027  label="SketchButtonCarve"
  AttachmentOffset = pos=(10,28.6,0) rot=(0,0,1;-0.314159rad)
  FullyConstrained = true
  MapMode = 5
  Placement = pos=(-4.1e-15,10,28.6) rot=(-0.506732,-0.697457,-0.506732;4.35963rad)
  Support = -> [YZ_Plane005]
  expr: .AttachmentOffset.Base.x = <<param>>.button_offset
  expr: .AttachmentOffset.Base.y = <<param>>.button_height - 2
  expr: .AttachmentOffset.Rotation.Angle = <<param>>.button_angle
  expr: Constraints[12] = <<param>>.button_hole / 2 + 10
  expr: Constraints[6] = <<param>>.button_hole / 2 + 4
  sketch-geometry (4):
    g0: LineSegment StartX=0 StartY=2 StartZ=0 EndX=12.2 EndY=2 EndZ=0
    g1: ArcOfCircle CenterX=18.2 CenterY=3.09999 CenterZ=0 NormalX=0 NormalY=0 NormalZ=1 AngleXU=0 Radius=6.09999 StartAngle=3.32291 EndAngle=4.71239
    g2: LineSegment StartX=0 StartY=2 StartZ=0 EndX=0 EndY=-3 EndZ=0
    g3: LineSegment StartX=18.2 StartY=-3 StartZ=0 EndX=0 EndY=-3 EndZ=0
  constraints (13):
    c: Horizontal(g0)
    c: Coincident(g1,g0)
    c: Coincident(g2,g0)
    c: Coincident(g3,g1)
    c: Horizontal(g3)
    c: Tangent(g3,g1)
    c: DistanceX(g0,g0) = 12.2
    c: DistanceY(g2,g2) = 5
    c: Coincident(g2,g3)
    c: Vertical(g2)
    c: PointOnObject(g-1,g2)
    c: DistanceY(g2,g-1) = 3
    c: DistanceX(g3,g3) = 18.2
FEATURE [Sketcher::SketchObject] Sketch028  label="SketchTerminals"
  FullyConstrained = true
  MapMode = 5
  Placement = pos=(0,0,0) rot=(1,0,0;1.5708rad)
  Support = -> [XZ_Plane005]
  expr: Constraints[17] = <<param>>.terminal_thickness
  expr: Constraints[18] = <<param>>.terminal_height
  expr: Constraints[21] = <<param>>.bottom_height
  expr: Constraints[22] = <<param>>.terminal_offset
  expr: Constraints[23] = <<param>>.terminal_seperation
  sketch-geometry (17):
    g0: LineSegment StartX=10.25 StartY=-12.9 StartZ=0 EndX=11.25 EndY=-12.9 EndZ=0
    g1: LineSegment StartX=11.25 StartY=-12.9 StartZ=0 EndX=11.25 EndY=-19.5 EndZ=0
    g2: LineSegment StartX=11.25 StartY=-19.5 StartZ=0 EndX=10.25 EndY=-19.5 EndZ=0
    g3: LineSegment StartX=10.25 StartY=-19.5 StartZ=0 EndX=10.25 EndY=-17.25 EndZ=0
    g4: LineSegment StartX=-10.25 StartY=-12.9 StartZ=0 EndX=-11.25 EndY=-12.9 EndZ=0
    g5: LineSegment StartX=-11.25 StartY=-12.9 StartZ=0 EndX=-11.25 EndY=-19.5 EndZ=0
    g6: LineSegment StartX=-11.25 StartY=-19.5 StartZ=0 EndX=-10.25 EndY=-19.5 EndZ=0
    g7: LineSegment StartX=-10.25 StartY=-19.5 StartZ=0 EndX=-10.25 EndY=-17.25 EndZ=0
    g8: Circle CenterX=0 CenterY=-24 CenterZ=0 NormalX=0 NormalY=0 NormalZ=1 AngleXU=0 Radius=3
    g9: LineSegment StartX=-10.25 StartY=-15.15 StartZ=0 EndX=-8.75 EndY=-15.15 EndZ=0
    g10: LineSegment StartX=-8.75 StartY=-15.15 StartZ=0 EndX=-8.75 EndY=-17.25 EndZ=0
    g11: LineSegment StartX=-8.75 StartY=-17.25 StartZ=0 EndX=-10.25 EndY=-17.25 EndZ=0
    g12: LineSegment StartX=-10.25 StartY=-15.15 StartZ=0 EndX=-10.25 EndY=-12.9 EndZ=0
    g13: LineSegment StartX=10.25 StartY=-15.15 StartZ=0 EndX=8.75 EndY=-15.15 EndZ=0
    g14: LineSegment StartX=8.75 StartY=-15.15 StartZ=0 EndX=8.75 EndY=-17.25 EndZ=0
    g15: LineSegment StartX=8.75 StartY=-17.25 StartZ=0 EndX=10.25 EndY=-17.25 EndZ=0
    g16: LineSegment StartX=10.25 StartY=-15.15 StartZ=0 EndX=10.25 EndY=-12.9 EndZ=0
  constraints (48):
    c: Coincident(g0,g1)
    c: Coincident(g1,g2)
    c: Coincident(g2,g3)
    c: Coincident(g16,g0)
    c: Horizontal(g0)
    c: Horizontal(g2)
    c: Vertical(g1)
    c: Vertical(g3)
    c: Coincident(g4,g5)
    c: Coincident(g5,g6)
    c: Coincident(g6,g7)
    c: Coincident(g12,g4)
    c: Horizontal(g4)
    c: Horizontal(g6)
    c: Vertical(g5)
    c: Vertical(g7)
    c: Equal(g4,g0)
    c: DistanceX(g4,g4) = 1
    c: DistanceY(g3,g16) = 6.6
    c: PointOnObject(g8,g-2)
    c: Radius(g8) = 3
    c: DistanceY(g8,g-1) = 24
    c: DistanceY(g8,g1) = 4.5
    c: DistanceX(g6,g1) = 21.5
    c: Symmetric(g4,g0,g-2)
    c: Horizontal(g9)
    c: Coincident(g10,g9)
    c: Vertical(g10)
    c: Coincident(g11,g10)
    c: Horizontal(g11)
    c: Coincident(g7,g11)
    c: Coincident(g12,g9)
    c: Tangent(g7,g12)
    c: Equal(g12,g7)
    c: Horizontal(g5,g1)
    c: DistanceY(g10,g10) = 2.1
    c: DistanceX(g9,g9) = 1.5
    c: Horizontal(g13)
    c: Coincident(g14,g13)
    c: Vertical(g14)
    c: Coincident(g15,g14)
    c: Horizontal(g15)
    c: Coincident(g3,g15)
    c: Coincident(g16,g13)
    c: Tangent(g3,g16)
    c: Equal(g16,g3)
    c: Equal(g13,g9)
    c: Equal(g14,g10)
FEATURE [Sketcher::SketchObject] Sketch029  label="SketchAccess"
  AttachmentOffset = pos=(0,0,-20.5) rot=(0,0,1;0rad)
  FullyConstrained = true
  MapMode = 5
  Placement = pos=(0,0,-20.5) rot=(0,0,1;0rad)
  Support = -> [XY_Plane005]
  expr: .AttachmentOffset.Base.z = -<<param>>.bottom_height + <<param>>.terminal_offset - 1
  expr: Constraints[19] = <<param>>.mid_depth / 2
  expr: Constraints[22] = <<param>>.terminal_seperation + <<param>>.terminal_thickness * 2
  expr: Constraints[23] = <<param>>.terminal_depth
  sketch-geometry (12):
    g0: LineSegment StartX=-11.75 StartY=41 StartZ=0 EndX=-11.75 EndY=18.5 EndZ=0
    g1: LineSegment StartX=-11.75 StartY=18.5 StartZ=0 EndX=-9.25 EndY=18.5 EndZ=0
    g2: LineSegment StartX=-7.95 StartY=21 StartZ=0 EndX=-7.95 EndY=41 EndZ=0
    g3: LineSegment StartX=-7.95 StartY=41 StartZ=0 EndX=-11.75 EndY=41 EndZ=0
    g4: LineSegment StartX=7.95 StartY=41 StartZ=0 EndX=11.75 EndY=41 EndZ=0
    g5: LineSegment StartX=11.75 StartY=41 StartZ=0 EndX=11.75 EndY=18.5 EndZ=0
    g6: LineSegment StartX=11.75 StartY=18.5 StartZ=0 EndX=9.25 EndY=18.5 EndZ=0
    g7: LineSegment StartX=7.95 StartY=21 StartZ=0 EndX=7.95 EndY=41 EndZ=0
    g8: LineSegment StartX=9.25 StartY=18.5 StartZ=0 EndX=9.25 EndY=19.5 EndZ=0
    g9: LineSegment StartX=7.95 StartY=21 StartZ=0 EndX=9.25 EndY=19.5 EndZ=0
    g10: LineSegment StartX=-9.25 StartY=18.5 StartZ=0 EndX=-9.25 EndY=19.5 EndZ=0
    g11: LineSegment StartX=-9.25 StartY=19.5 StartZ=0 EndX=-7.95 EndY=21 EndZ=0
  constraints (35):
    c: Vertical(g0)
    c: Coincident(g0,g1)
    c: Vertical(g2)
    c: Coincident(g2,g3)
    c: Coincident(g3,g0)
    c: Horizontal(g3)
    c: Horizontal(g4)
    c: Coincident(g4,g5)
    c: Vertical(g5)
    c: Coincident(g5,g6)
    c: Horizontal(g6)
    c: Coincident(g7,g4)
    c: Vertical(g7)
    c: Equal(g3,g4)
    c: Equal(g0,g5)
    c: Horizontal(g1)
    c: Equal(g2,g7)
    c: Equal(g1,g6)
    c: Symmetric(g2,g4,g-2)
    c: DistanceY(g-1,g0) = 41
    c: DistanceX(g1,g1) = 2.5
    c: DistanceX(g0,g2) = 3.8
    c: DistanceX(g0,g5) = 23.5
    c: DistanceY(g5,g4) = 22.5
    c: DistanceY(g2,g2) = 20
    c: Coincident(g8,g6) = 23.5
    c: Vertical(g8) = 22
    c: Coincident(g9,g7)
    c: Coincident(g9,g8)
    c: Coincident(g10,g1)
    c: Coincident(g11,g10)
    c: Coincident(g11,g2)
    c: Equal(g8,g10)
    c: DistanceY(g8,g8) = 1
    c: Vertical(g10)
FEATURE [Sketcher::SketchObject] Sketch030  label="SketchFront"
  AttachmentOffset = pos=(0,0,41) rot=(0,0,1;0rad)
  FullyConstrained = true
  MapMode = 5
  Placement = pos=(0,-41,-9.1e-15) rot=(1,0,0;1.5708rad)
  Support = -> [XZ_Plane006]
  expr: .AttachmentOffset.Base.z = <<param>>.mid_depth / 2
  expr: Constraints[16] = <<param>>.radius_big * 1.2
  expr: Constraints[21] = <<param>>.radius_big
  expr: Constraints[2] = <<param>>.bottom_width
  expr: Constraints[4] = <<param>>.bottom_height + 10
  expr: Constraints[5] = <<param>>.front_width2
  expr: Constraints[6] = <<param>>.front_width2
  expr: Constraints[7] = <<param>>.front_height + 20
  sketch-geometry (10):
    g0: LineSegment StartX=-47.5 StartY=56 StartZ=0 EndX=47.5 EndY=56 EndZ=0
    g1: LineSegment StartX=47.5 StartY=56 StartZ=0 EndX=47.5 EndY=10.5451 EndZ=0
    g2: LineSegment StartX=36 StartY=-8.78755 StartZ=0 EndX=36 EndY=-34 EndZ=0
    g3: LineSegment StartX=36 StartY=-34 StartZ=0 EndX=-36 EndY=-34 EndZ=0
    g4: LineSegment StartX=-36 StartY=-34 StartZ=0 EndX=-36 EndY=-8.78755 EndZ=0
    g5: LineSegment StartX=-47.5 StartY=10.5451 StartZ=0 EndX=-47.5 EndY=56 EndZ=0
    g6: ArcOfCircle CenterX=46 CenterY=-8.78755 CenterZ=0 NormalX=0 NormalY=0 NormalZ=1 AngleXU=0 Radius=10 StartAngle=2.06834 EndAngle=3.14159
    g7: ArcOfCircle CenterX=35.5 CenterY=10.5451 CenterZ=0 NormalX=0 NormalY=0 NormalZ=1 AngleXU=0 Radius=12 StartAngle=5.20994 EndAngle=6.28319
    g8: ArcOfCircle CenterX=-46 CenterY=-8.78755 CenterZ=0 NormalX=0 NormalY=0 NormalZ=1 AngleXU=0 Radius=10 StartAngle=0 EndAngle=1.07325
    g9: ArcOfCircle CenterX=-35.5 CenterY=10.5451 CenterZ=0 NormalX=0 NormalY=0 NormalZ=1 AngleXU=0 Radius=12 StartAngle=3.14159 EndAngle=4.21484
  constraints (26):
    c: Vertical(g2)
    c: Vertical(g4)
    c: DistanceX(g4,g2) = 72
    c: Symmetric(g3,g3,g-2)
    c: DistanceY(g3,g-1) = 34
    c: DistanceX(g5,g1) = 95
    c: DistanceX(g5,g1) = 95
    c: DistanceY(g3,g0) = 90
    c: Equal(g8,g6)
    c: Symmetric(g5,g1,g-2)
    c: Equal(g4,g2)
    c: Coincident(g6,g2)
    c: Coincident(g0,g1)
    c: Coincident(g5,g0)
    c: Symmetric(g0,g0,g-2)
    c: Equal(g7,g9)
    c: Radius(g7) = 12
    c: Tangent(g9,g5) = 1.5708
    c: Tangent(g1,g7) = 1.5708
    c: Tangent(g9,g8) = 1.5708
    c: Tangent(g6,g7) = 1.5708
    c: Radius(g6) = 10
    c: DistanceY(g6,g-1) = 0
    c: Tangent(g8,g4) = -1.5708
    c: Coincident(g3,g2)
    c: Coincident(g3,g4)
FEATURE [Sketcher::SketchObject] Sketch031  label="SketchRear"
  AttachmentOffset = pos=(0,0,-46) rot=(0,0,1;0rad)
  FullyConstrained = true
  MapMode = 5
  Placement = pos=(0,46,1.02e-14) rot=(1,0,0;1.5708rad)
  Support = -> [XZ_Plane006]
  expr: .AttachmentOffset.Base.z = -<<param>>.mid_depth / 2 - <<param>>.back_thickness
  expr: Constraints[1] = <<param>>.bottom_height + 10
  expr: Constraints[2] = <<param>>.rear_width
  expr: Constraints[6] = <<param>>.front_height + 20
  sketch-geometry (4):
    g0: LineSegment StartX=-36 StartY=-34 StartZ=0 EndX=36 EndY=-34 EndZ=0
    g1: LineSegment StartX=36 StartY=56 StartZ=0 EndX=-36 EndY=56 EndZ=0
    g2: LineSegment StartX=36 StartY=-34 StartZ=0 EndX=36 EndY=56 EndZ=0
    g3: LineSegment StartX=-36 StartY=-34 StartZ=0 EndX=-36 EndY=56 EndZ=0
  constraints (12):
    c: Horizontal(g0)
    c: DistanceY(g0,g-1) = 34
    c: DistanceX(g3,g2) = 72
    c: Vertical(g2)
    c: Equal(g3,g2)
    c: Vertical(g3)
    c: DistanceY(g0,g1) = 90
    c: Symmetric(g2,g3,g-2)
    c: Coincident(g2,g1)
    c: Coincident(g3,g1)
    c: Coincident(g2,g0)
    c: Equal(g1,g0)
FEATURE [Part::Plane] Plane002  label="PlaneDivider"
  AttacherType = Attacher::AttachEngine3D
  Length = 152
  Placement = pos=(-75,41,-75) rot=(1,0,0;1.5708rad)
  Support = -> [XZ_Plane006]
  Width = 150
  expr: .Placement.Base.y = <<param>>.mid_depth / 2
FEATURE [Sketcher::SketchObject] Sketch032  label="SketchBack"
  FullyConstrained = true
  MapMode = 5
  Placement = pos=(0,0,0) rot=(1,0,0;1.5708rad)
  Support = -> [XZ_Plane]
  expr: Constraints[10] = <<param>>.rear_screw_width1
  expr: Constraints[11] = <<param>>.reart_screw_width2
  expr: Constraints[12] = <<param>>.rear_screw_height
  expr: Constraints[15] = <<param>>.rear_screw_offset
  expr: Constraints[1] = <<param>>.bottom_height
  expr: Constraints[2] = <<param>>.rear_width
  expr: Constraints[9] = <<param>>.screw_hole + 1
  sketch-geometry (6):
    g0: LineSegment StartX=36 StartY=-24 StartZ=0 EndX=-36 EndY=-24 EndZ=0
    g1: Circle CenterX=-29 CenterY=14.9 CenterZ=0 NormalX=0 NormalY=0 NormalZ=1 AngleXU=0 Radius=1.75
    g2: Circle CenterX=0 CenterY=14.9 CenterZ=0 NormalX=0 NormalY=0 NormalZ=1 AngleXU=0 Radius=1.75
    g3: Circle CenterX=29 CenterY=14.9 CenterZ=0 NormalX=0 NormalY=0 NormalZ=1 AngleXU=0 Radius=1.75
    g4: Circle CenterX=-27.5 CenterY=-16.6 CenterZ=0 NormalX=0 NormalY=0 NormalZ=1 AngleXU=0 Radius=1.75
    g5: Circle CenterX=27.5 CenterY=-16.6 CenterZ=0 NormalX=0 NormalY=0 NormalZ=1 AngleXU=0 Radius=1.75
  constraints (16):
    c: Symmetric(g0,g0,g-2)
    c: DistanceY(g0,g-1) = 24
    c: DistanceX(g0,g0) = 72
    c: Symmetric(g1,g3,g-2)
    c: Symmetric(g4,g5,g-2)
    c: Equal(g4,g1)
    c: Equal(g1,g2)
    c: Equal(g2,g3)
    c: Equal(g3,g5)
    c: Diameter(g1) = 3.5
    c: DistanceX(g1,g3) = 58
    c: DistanceX(g4,g5) = 55
    c: DistanceY(g5,g3) = 31.5
    c: Horizontal(g1,g2)
    c: PointOnObject(g2,g-2)
    c: DistanceY(g0,g5) = 7.4
FEATURE [Part::Loft] Loft
  Closed = false
  MaxDegree = 5
  Ruled = false
  Sections = -> [Sketch030,Sketch031]
  Solid = true
FEATURE [Part::Extrusion] Extrude
  Base = -> Sketch012
  Dir = (1,-1e-16,1e-16)
  DirMode = 2
  FaceMakerClass = Part::FaceMakerBullseye
  LengthFwd = 100
  LengthRev = 0
  Solid = true
  Symmetric = true
FEATURE [Part::MultiCommon] Common
  Shapes = -> [Extrude,Loft]
FEATURE [Part::FeaturePython] Slice  # WARN: FeaturePython — macro-defined, semantics opaque (R4)
  Base = -> Common
  Mode = 1
  Tolerance = 0
  Tools = -> [Plane002]
FEATURE [Part::FeaturePython] Slice_child0  label="Slice.Case"  # WARN: FeaturePython — macro-defined, semantics opaque (R4)
  Base = -> Slice
  FilterType = 1
  Invert = false
  OverrideMaxVal = 0
  WindowFrom = 80
  WindowTo = 100
  items = 0
FEATURE [Part::FeaturePython] Slice_child1  label="Slice.Back"  # WARN: FeaturePython — macro-defined, semantics opaque (R4)
  Base = -> Slice
  FilterType = 1
  Invert = false
  OverrideMaxVal = 0
  WindowFrom = 80
  WindowTo = 100
  items = 1
FEATURE [App::DocumentObjectGroup] GrExplode_Slice  label="Exploded Slice"
  Group = -> [Slice_child0,Slice_child1]
FEATURE [App::DocumentObjectGroup] Group001  label="BaseShape"
  Group = -> [Common,Sketch012,Sketch031,Sketch030,Plane002,GrExplode_Slice]
FEATURE [PartDesign::FeatureBase] BaseFeature  label="Back.BaseFeature"
  BaseFeature = -> Slice_child1
FEATURE [PartDesign::Pocket] Pocket  label="Back.Pocket.Screws"
  BaseFeature = -> BaseFeature
  Direction = (0,1,2e-16)
  Length = 5
  Length2 = 100
  Midplane = true
  Profile = -> Sketch032
  Type = 1
FEATURE [PartDesign::FeatureBase] BaseFeature001  label="Case.BaseFeature"
  BaseFeature = -> Slice_child0
FEATURE [PartDesign::Pocket] Pocket001  label="Case.Pocket.Batt"
  BaseFeature = -> BaseFeature001
  Direction = (0,0,-1)
  Length = 14.6
  Length2 = 100
  Profile = -> Sketch018
  Reversed = true
  Type = 0
  expr: Length = <<param>>.batt_carveout
FEATURE [PartDesign::Pad] Pad  label="Case.Pad.Batt"
  BaseFeature = -> Pocket001
  Direction = (0,-1,-2e-16)
  Length = 45
  Length2 = 100
  Profile = -> Sketch019
  Type = 0
  expr: Length = <<param>>.batt_rail_length
FEATURE [PartDesign::Pocket] Pocket002  label="Case.Pocket.Support"
  BaseFeature = -> Pad
  Direction = (0,1,2e-16)
  Length = 5
  Length2 = 100
  Profile = -> Sketch
  Type = 0
FEATURE [PartDesign::Pocket] Pocket006  label="Case.Pocket.Terminal"
  BaseFeature = -> Pocket002
  Direction = (0,1,2e-16)
  Length = 18.5
  Length2 = 100
  Profile = -> Sketch028
  Type = 0
  expr: Length = <<param>>.mid_depth / 2 - <<param>>.terminal_depth
FEATURE [PartDesign::Pocket] Pocket005  label="Case.Pocket.Access"
  BaseFeature = -> Pocket006
  Direction = (0,0,-1)
  Length = 22.5
  Length2 = 100
  Profile = -> Sketch029
  Reversed = true
  Type = 0
  expr: Length = <<param>>.terminal_depth
FEATURE [Sketcher::SketchObject] Sketch033  label="SketchFace"
  FullyConstrained = true
  MapMode = 5
  Placement = pos=(0,0,0) rot=(1,0,0;1.5708rad)
  Support = -> [XZ_Plane007]
  expr: Constraints[12] = <<param>>.face_radius
  expr: Constraints[21] = <<param>>.face_width1 - <<param>>.face_fit
  expr: Constraints[22] = <<param>>.face_width2 - <<param>>.face_fit
  expr: Constraints[23] = <<param>>.face_height - <<param>>.face_fit
  expr: Constraints[27] = <<param>>.screw_hole + 1
  expr: Constraints[28] = <<param>>.front_screw_width2 / 2
  expr: Constraints[29] = <<param>>.front_screw_width2 / 2
  expr: Constraints[30] = <<param>>.front_screw_width1 / 2
  expr: Constraints[31] = <<param>>.front_screw_width1 / 2
  expr: Constraints[32] = <<param>>.front_screw_height
  expr: Constraints[35] = <<param>>.front_screw_offset
  expr: Constraints[50] = <<param>>.face_plug_hole
  expr: Constraints[51] = <<param>>.face_knob_hole
  expr: Constraints[55] = <<param>>.face_screen_height
  expr: Constraints[56] = <<param>>.face_screen_width
  expr: Constraints[57] = <<param>>.face_screen_radius
  expr: Constraints[58] = <<param>>.face_screen_x
  expr: Constraints[60] = <<param>>.face_knob_y
  expr: Constraints[61] = <<param>>.face_knob_x
  expr: Constraints[65] = <<param>>.face_plug_y
  expr: Constraints[66] = <<param>>.face_plug_x
  sketch-geometry (23):
    g0: LineSegment StartX=-34.3037 StartY=40.6 StartZ=0 EndX=34.3037 EndY=40.6 EndZ=0
    g1: LineSegment StartX=42.3 StartY=32.8438 StartZ=0 EndX=43.05 EndY=8.24381 EndZ=0
    g2: LineSegment StartX=35.0537 StartY=7.168e-13 StartZ=0 EndX=-35.0537 EndY=1.039e-13 EndZ=0
    g3: LineSegment StartX=-43.05 StartY=8.24381 StartZ=0 EndX=-42.3 EndY=32.8438 EndZ=0
    g4: ArcOfCircle CenterX=34.3037 CenterY=32.6 CenterZ=0 NormalX=0 NormalY=0 NormalZ=1 AngleXU=0 Radius=8 StartAngle=0.030479 EndAngle=1.5708
    g5: ArcOfCircle CenterX=35.0537 CenterY=8 CenterZ=0 NormalX=0 NormalY=0 NormalZ=1 AngleXU=0 Radius=8 StartAngle=4.71239 EndAngle=6.31367
    g6: ArcOfCircle CenterX=-34.3037 CenterY=32.6 CenterZ=0 NormalX=0 NormalY=0 NormalZ=1 AngleXU=0 Radius=8 StartAngle=1.5708 EndAngle=3.11111
    g7: ArcOfCircle CenterX=-35.0537 CenterY=8 CenterZ=0 NormalX=0 NormalY=0 NormalZ=1 AngleXU=0 Radius=8 StartAngle=3.11111 EndAngle=4.71239
    g8: Circle CenterX=-36.75 CenterY=35.5 CenterZ=0 NormalX=0 NormalY=0 NormalZ=1 AngleXU=0 Radius=1.75
    g9: Circle CenterX=36.75 CenterY=35.5 CenterZ=0 NormalX=0 NormalY=0 NormalZ=1 AngleXU=0 Radius=1.75
    g10: Circle CenterX=-38 CenterY=5.5 CenterZ=0 NormalX=0 NormalY=0 NormalZ=1 AngleXU=0 Radius=1.75
    g11: Circle CenterX=38 CenterY=5.5 CenterZ=0 NormalX=0 NormalY=0 NormalZ=1 AngleXU=0 Radius=1.75
    g12: LineSegment StartX=-14 StartY=30.95 StartZ=0 EndX=14 EndY=30.95 EndZ=0
    g13: LineSegment StartX=16 StartY=28.95 StartZ=0 EndX=16 EndY=16.45 EndZ=0
    g14: LineSegment StartX=14 StartY=14.45 StartZ=0 EndX=-14 EndY=14.45 EndZ=0
    g15: LineSegment StartX=-16 StartY=16.45 StartZ=0 EndX=-16 EndY=28.95 EndZ=0
    g16: ArcOfCircle CenterX=-14 CenterY=28.95 CenterZ=0 NormalX=0 NormalY=0 NormalZ=1 AngleXU=0 Radius=2 StartAngle=1.5708 EndAngle=3.14159
    g17: ArcOfCircle CenterX=-14 CenterY=16.45 CenterZ=0 NormalX=0 NormalY=0 NormalZ=1 AngleXU=0 Radius=2 StartAngle=3.14159 EndAngle=4.71239
    g18: ArcOfCircle CenterX=14 CenterY=16.45 CenterZ=0 NormalX=0 NormalY=0 NormalZ=1 AngleXU=0 Radius=2 StartAngle=4.71239 EndAngle=6.28319
    g19: ArcOfCircle CenterX=14 CenterY=28.95 CenterZ=0 NormalX=0 NormalY=0 NormalZ=1 AngleXU=0 Radius=2 StartAngle=1e-16 EndAngle=1.5708
    g20: Circle CenterX=-31 CenterY=18.7 CenterZ=0 NormalX=0 NormalY=0 NormalZ=1 AngleXU=0 Radius=7.75
    g21: Circle CenterX=31 CenterY=22.7 CenterZ=0 NormalX=0 NormalY=0 NormalZ=1 AngleXU=0 Radius=3.6
    g22: LineSegment StartX=-69 StartY=22.7 StartZ=0 EndX=31 EndY=22.7 EndZ=0
  constraints (67):
    c: Coincident(g4,g0)
    c: Coincident(g4,g1)
    c: Coincident(g5,g1)
    c: Coincident(g5,g2)
    c: Coincident(g6,g0)
    c: Coincident(g6,g3)
    c: Coincident(g7,g3)
    c: Coincident(g7,g2)
    c: Equal(g1,g3)
    c: Equal(g4,g6)
    c: Equal(g6,g7)
    c: Equal(g7,g5)
    c: Radius(g4) = 8
    c: Tangent(g6,g3)
    c: Tangent(g7,g3)
    c: Tangent(g7,g2)
    c: Tangent(g6,g0)
    c: Tangent(g4,g0)
    c: Tangent(g4,g1)
    c: Tangent(g5,g1)
    c: Tangent(g5,g2)
    c: DistanceX(g3,g1) = 84.6
    c: DistanceX(g3,g1) = 86.1
    c: DistanceY(g2,g0) = 40.6
    c: Equal(g9,g8)
    c: Equal(g8,g10)
    c: Equal(g10,g11)
    c: Diameter(g8) = 3.5
    c: DistanceX(g10,g-1) = 38
    c: DistanceX(g-1,g11) = 38
    c: DistanceX(g-1,g9) = 36.75
    c: DistanceX(g8,g-1) = 36.75
    c: DistanceY(g11,g9) = 30
    c: Horizontal(g8,g9)
    c: Horizontal(g10,g11)
    c: DistanceY(g-1,g11) = 5.5
    c: Horizontal(g12)
    c: Horizontal(g14)
    c: Vertical(g13)
    c: Vertical(g15)
    c: Tangent(g15,g16) = 1.5708
    c: Tangent(g12,g16) = 1.5708
    c: Tangent(g15,g17) = 1.5708
    c: Tangent(g14,g17) = 1.5708
    c: Tangent(g14,g18) = 1.5708
    c: Tangent(g13,g18) = 1.5708
    c: Tangent(g12,g19) = 1.5708
    c: Tangent(g13,g19) = 1.5708
    c: Horizontal(g0)
    c: Symmetric(g2,g2,g-2)
    c: Diameter(g20) = 15.5
    c: Diameter(g21) = 7.2
    c: Equal(g16,g17)
    c: Equal(g17,g18)
    c: Equal(g18,g19)
    c: DistanceY(g14,g12) = 16.5
    c: DistanceX(g15,g13) = 32
    c: Radius(g19) = 2
    c: DistanceX(g13,g21) = 15
    c: Symmetric(g12,g14,g22)
    c: DistanceY(g-1,g22) = 22.7
    c: DistanceX(g-1,g21) = 31
    c: DistanceX(g22,g22) = 100
    c: Coincident(g22,g21)
    c: PointOnObject(g-1,g2)
    c: Distance(g20,g-1) = 18.7
    c: Distance(g20,g-2) = 31
FEATURE [PartDesign::Pad] Pad001  label="Face.Pad.Face"
  Direction = (0,-1,-2e-16)
  Length = 3
  Length2 = 100
  Placement = pos=(0,0,0) rot=(1,0,0;1.5708rad)
  Profile = -> Sketch033
  Type = 0
  expr: Length = <<param>>.face_thickness
FEATURE [PartDesign::Chamfer] Chamfer001  label="Face.Chamfer.Screen"
  Angle = 45
  Base = -> Pad001 [Edge34]
  BaseFeature = -> Pad001
  ChamferType = 0
  FlipDirection = false
  Placement = pos=(0,0,0) rot=(1,0,0;1.5708rad)
  Size = 2
  Size2 = 1
  SupportTransform = false
  UseAllEdges = false
FEATURE [PartDesign::Chamfer] Chamfer002  label="Face.Chamfer.Screws"
  Angle = 45
  Base = -> Chamfer001 [Edge54,Edge56,Edge53,Edge55]
  BaseFeature = -> Chamfer001
  ChamferType = 0
  FlipDirection = false
  Placement = pos=(0,0,0) rot=(1,0,0;1.5708rad)
  Size = 1.4
  Size2 = 1
  SupportTransform = false
  UseAllEdges = false
FEATURE [Sketcher::SketchObject] Sketch034  label="SketchRing"
  FullyConstrained = true
  MapMode = 5
  Placement = pos=(0,0,0) rot=(1,0,0;1.5708rad)
  Support = -> [XZ_Plane008]
  sketch-geometry (6):
    g0: LineSegment StartX=-1 StartY=6.25 StartZ=0 EndX=1 EndY=6.25 EndZ=0
    g1: LineSegment StartX=1 StartY=6.25 StartZ=0 EndX=1 EndY=7.75 EndZ=0
    g2: LineSegment StartX=1 StartY=7.75 StartZ=0 EndX=0.3 EndY=7.75 EndZ=0
    g3: LineSegment StartX=0.3 StartY=7.75 StartZ=0 EndX=0.3 EndY=8.75 EndZ=0
    g4: LineSegment StartX=0.3 StartY=8.75 StartZ=0 EndX=-1 EndY=8.75 EndZ=0
    g5: LineSegment StartX=-1 StartY=8.75 StartZ=0 EndX=-1 EndY=6.25 EndZ=0
  constraints (17):
    c: Coincident(g0,g1)
    c: Vertical(g1)
    c: Coincident(g1,g2)
    c: Horizontal(g2)
    c: Coincident(g2,g3)
    c: Vertical(g3)
    c: Coincident(g3,g4)
    c: Horizontal(g4)
    c: Coincident(g4,g5)
    c: Coincident(g5,g0)
    c: Vertical(g5)
    c: DistanceX(g0,g0) = 2
    c: DistanceY(g3,g3) = 1
    c: DistanceX(g4,g4) = 1.3
    c: Symmetric(g0,g0,g-2)
    c: DistanceY(g-1,g0) = 6.25
    c: DistanceY(g5,g5) = 2.5
FEATURE [PartDesign::Revolution] Revolution001  label="Ring.Revolution"
  Angle = 360
  Axis = (1,0,0)
  Base = (0,0,0)
  Placement = pos=(0,0,0) rot=(1,0,0;1.5708rad)
  Profile = -> Sketch034
  ReferenceAxis = -> X_Axis008
FEATURE [PartDesign::Body] Body006  label="BodyRing"
  Group = -> [Sketch034,Revolution001]
  Origin = -> Origin008
  Tip = -> Revolution001
FEATURE [Part::Box] Box  label="Cube"
  AttacherType = Attacher::AttachEngine3D
  Height = 18
  Length = 18
  Placement = pos=(-9,-0.25,-9) rot=(0,0,1;0rad)
  Width = 0.5
FEATURE [Part::FeaturePython] Slice001  # WARN: FeaturePython — macro-defined, semantics opaque (R4)
  Base = -> Body006
  Mode = 1
  Tolerance = 0
  Tools = -> [Box]
FEATURE [Part::FeaturePython] Slice001_child1  label="Slice001.Ring1"  # WARN: FeaturePython — macro-defined, semantics opaque (R4)
  Base = -> Slice001
  FilterType = 1
  Invert = false
  OverrideMaxVal = 0
  WindowFrom = 80
  WindowTo = 100
  items = 1
FEATURE [Part::FeaturePython] Slice001_child2  label="Slice001.Ring2"  # WARN: FeaturePython — macro-defined, semantics opaque (R4)
  Base = -> Slice001
  FilterType = 1
  Invert = false
  OverrideMaxVal = 0
  WindowFrom = 80
  WindowTo = 100
  items = 2
FEATURE [App::DocumentObjectGroup] GrExplode_Slice001  label="Ring.Exploded Slice"
  Group = -> [Slice001_child1,Slice001_child2]
FEATURE [Sketcher::SketchObject] Sketch035
  AttachmentOffset = pos=(0,0,1.5) rot=(1,0,0;0rad)
  ExternalGeometry = -> [Sketch033]
  FullyConstrained = true
  MapMode = 5
  Placement = pos=(0,-1.5,-3e-16) rot=(1,0,0;1.5708rad)
  Support = -> [XZ_Plane007]
  expr: .AttachmentOffset.Base.z = <<param>>.face_thickness - 1.5
  sketch-geometry (1):
    g0: Circle CenterX=-31 CenterY=18.7 CenterZ=0 NormalX=0 NormalY=0 NormalZ=1 AngleXU=0 Radius=9
  constraints (2):
    c: Coincident(g0,g-3)
    c: Diameter(g0) = 18
FEATURE [PartDesign::Pocket] Pocket008  label="Face.Pocket.Lip"
  BaseFeature = -> Chamfer002
  Direction = (0,1,2e-16)
  Length = 1.5
  Length2 = 100
  Placement = pos=(0,0,0) rot=(1,0,0;1.5708rad)
  Profile = -> Sketch035
  Reversed = true
  Type = 1
FEATURE [Sketcher::SketchObject] Sketch036
  ExternalGeometry = -> [Sketch033]
  FullyConstrained = true
  MapMode = 5
  Placement = pos=(0,0,0) rot=(1,0,0;1.5708rad)
  Support = -> [XZ_Plane007]
  sketch-geometry (5):
    g0: ArcOfCircle CenterX=30 CenterY=16.7 CenterZ=0 NormalX=0 NormalY=0 NormalZ=1 AngleXU=0 Radius=0.75 StartAngle=1.5708 EndAngle=4.71239
    g1: ArcOfCircle CenterX=32 CenterY=16.7 CenterZ=0 NormalX=0 NormalY=0 NormalZ=1 AngleXU=0 Radius=0.75 StartAngle=4.71239 EndAngle=7.85398
    g2: LineSegment StartX=30 StartY=15.95 StartZ=0 EndX=32 EndY=15.95 EndZ=0
    g3: LineSegment StartX=30 StartY=17.45 StartZ=0 EndX=32 EndY=17.45 EndZ=0
    g4: LineSegment StartX=31 StartY=22.7 StartZ=0 EndX=31 EndY=13.7 EndZ=0
  constraints (12):
    c: Tangent(g0,g3) = 1.5708
    c: Tangent(g0,g2) = -1.5708
    c: Tangent(g2,g1) = -1.5708
    c: Tangent(g3,g1) = 1.5708
    c: Horizontal(g2)
    c: Equal(g0,g1)
    c: DistanceY(g1,g-3) = 6
    c: DistanceY(g1,g1) = 1.5
    c: DistanceX(g0,g1) = 2
    c: Coincident(g4,g-3)
    c: Symmetric(g0,g1,g4)
    c: DistanceY(g4,g4) = 9
FEATURE [PartDesign::Pocket] Pocket009  label="Face.Pocket.Notch"
  BaseFeature = -> Pocket008
  Direction = (0,1,2e-16)
  Length = 1
  Length2 = 100
  Placement = pos=(0,0,0) rot=(1,0,0;1.5708rad)
  Profile = -> Sketch036
  Reversed = true
  Type = 0
FEATURE [PartDesign::Body] Body005  label="BodyFace"
  Group = -> [Sketch033,Pad001,Chamfer001,Chamfer002,Sketch035,Pocket008,Sketch036,Pocket009]
  Origin = -> Origin007
  Placement = pos=(0,-36.7,2.8) rot=(-1,0,0;0.349066rad)
  Tip = -> Pocket009
  expr: .Placement.Base.y = -<<param>>.mid_depth / 2 + 4.3
  expr: .Placement.Base.z = <<param>>.face_offset
  expr: .Placement.Rotation.Angle = <<param>>.front_angle
FEATURE [PartDesign::Fillet] Fillet  label="Back.Fillet.Big"
  Base = -> Pocket [Edge34,Edge32]
  BaseFeature = -> Pocket
  Radius = 10
  SupportTransform = false
  UseAllEdges = false
  expr: Radius = <<param>>.radius_big
FEATURE [Sketcher::SketchObject] Sketch037
  AttachmentOffset = pos=(0,0,-41) rot=(0,0,1;0rad)
  FullyConstrained = true
  MapMode = 5
  Placement = pos=(0,41,9.1e-15) rot=(1,0,0;1.5708rad)
  Support = -> [XZ_Plane005]
  expr: .AttachmentOffset.Base.z = -<<param>>.mid_depth / 2
  expr: Constraints[20] = <<param>>.reart_screw_width2
  expr: Constraints[23] = <<param>>.screw_hole / 2
  expr: Constraints[24] = <<param>>.rear_screw_offset
  expr: Constraints[2] = <<param>>.bottom_height
  sketch-geometry (9):
    g0: Circle CenterX=0 CenterY=-24 CenterZ=0 NormalX=0 NormalY=0 NormalZ=1 AngleXU=0 Radius=3
    g1: LineSegment StartX=4.5 StartY=-22.8 StartZ=0 EndX=4.5 EndY=-24 EndZ=0
    g2: LineSegment StartX=4.5 StartY=-24 StartZ=0 EndX=11.5 EndY=-24 EndZ=0
    g3: LineSegment StartX=11.5 StartY=-24 StartZ=0 EndX=11.5 EndY=-22.8 EndZ=0
    g4: ArcOfCircle CenterX=5.5 CenterY=-22.8 CenterZ=0 NormalX=0 NormalY=0 NormalZ=1 AngleXU=0 Radius=1 StartAngle=1.5708 EndAngle=3.14159
    g5: ArcOfCircle CenterX=10.5 CenterY=-22.8 CenterZ=0 NormalX=0 NormalY=0 NormalZ=1 AngleXU=0 Radius=1 StartAngle=-9e-16 EndAngle=1.5708
    g6: LineSegment StartX=5.5 StartY=-21.8 StartZ=0 EndX=10.5 EndY=-21.8 EndZ=0
    g7: Circle CenterX=-27.5 CenterY=-16.6 CenterZ=0 NormalX=0 NormalY=0 NormalZ=1 AngleXU=0 Radius=1.25
    g8: Circle CenterX=27.5 CenterY=-16.6 CenterZ=0 NormalX=0 NormalY=0 NormalZ=1 AngleXU=0 Radius=1.25
  constraints (25):
    c: PointOnObject(g0,g-2)
    c: Radius(g0) = 3
    c: DistanceY(g0,g-1) = 24
    c: Vertical(g1)
    c: Coincident(g1,g2)
    c: Horizontal(g2)
    c: Coincident(g2,g3)
    c: Coincident(g5,g3)
    c: Horizontal(g6)
    c: Vertical(g3)
    c: Horizontal(g0,g1)
    c: DistanceX(g0,g1) = 4.5
    c: Equal(g3,g1)
    c: Equal(g4,g5)
    c: Radius(g5) = 1
    c: Tangent(g6,g4) = 1.5708
    c: Tangent(g6,g5) = 1.5708
    c: Tangent(g4,g1) = -1.5708
    c: DistanceY(g2,g5) = 2.2
    c: DistanceX(g1,g2) = 7
    c: DistanceX(g7,g8) = 55
    c: Symmetric(g7,g8,g-2)
    c: Equal(g7,g8)
    c: Radius(g7) = 1.25
    c: DistanceY(g0,g7) = 7.4
FEATURE [PartDesign::Pocket] Pocket010  label="Case.Pocket.Key"
  BaseFeature = -> Pocket005
  Direction = (0,1,2e-16)
  Length = 0
  Length2 = 100
  Midplane = true
  Profile = -> Sketch037
  Type = 3
  UpToFace = -> Pocket005 [Face20]
FEATURE [PartDesign::SubtractiveLoft] SubtractiveLoft  label="Case.SubtractiveLoft"
  BaseFeature = -> Pocket010
  Closed = false
  Profile = -> Sketch022
  Ruled = true
  Sections = -> [Sketch025,Sketch023]
FEATURE [PartDesign::Revolution] Revolution  label="Case.Revolution.Button"
  Angle = 360
  Axis = (-1e-16,0.309017,0.951057)
  Base = (-4.6e-15,10,30.6)
  BaseFeature = -> SubtractiveLoft
  Profile = -> Sketch021
  ReferenceAxis = -> Sketch021 [V_Axis]
  Reversed = true
FEATURE [PartDesign::Pocket] Pocket007  label="Case.Pocket.Button"
  BaseFeature = -> Revolution
  Direction = (0,-0.309017,-0.951057)
  Length = 14
  Length2 = 100
  Profile = -> Sketch008
  Reversed = true
  Type = 0
FEATURE [PartDesign::Groove] Groove  label="Case.Groove.Button"
  Angle = 360
  Axis = (-1e-16,0.309017,0.951057)
  Base = (-4.1e-15,10,28.6)
  BaseFeature = -> Pocket007
  Profile = -> Sketch027
  ReferenceAxis = -> Sketch027 [V_Axis]
FEATURE [PartDesign::Pocket] Pocket004  label="Case.Pocket.Screws"
  BaseFeature = -> Groove
  Direction = (0,0.939693,-0.34202)
  Length = 5
  Length2 = 100
  Profile = -> Sketch026
  Type = 0
FEATURE [PartDesign::Fillet] Fillet008  label="Case.Fillet.Button"
  Base = -> Pocket004 [Edge174]
  BaseFeature = -> Pocket004
  Radius = 10
  SupportTransform = false
  UseAllEdges = false
FEATURE [PartDesign::Pocket] Pocket003  label="Case.Pocket.Face"
  BaseFeature = -> Fillet008
  Direction = (0,0.939693,-0.34202)
  Length = 6
  Length2 = 100
  Profile = -> Sketch024
  Reversed = true
  Type = 0
  expr: Length = <<param>>.face_thickness * 2
FEATURE [PartDesign::Fillet] Fillet005  label="Case.Fillet.Top"
  Base = -> Pocket003 [Edge2,Edge5]
  BaseFeature = -> Pocket003
  Radius = 10
  SupportTransform = false
  UseAllEdges = false
  expr: Radius = <<param>>.radius_big
FEATURE [Mesh::Feature] Mesh006  label="SliceRing (Meshed)"
FEATURE [Mesh::Feature] Mesh007  label="BodyFace (Meshed)"
FEATURE [PartDesign::Fillet] Fillet009  label="Back.Fillet.Bottom"
  Base = -> Fillet [Edge32,Edge37]
  BaseFeature = -> Fillet
  Radius = 3
  SupportTransform = false
  UseAllEdges = false
  expr: Radius = <<param>>.radius_medium
FEATURE [PartDesign::Fillet] Fillet004  label="Back.Fillet.Rear"
  Base = -> Fillet009 [Edge42]
  BaseFeature = -> Fillet009
  Radius = 3
  SupportTransform = false
  UseAllEdges = false
  expr: Radius = <<param>>.radius_medium
FEATURE [PartDesign::Chamfer] Chamfer  label="Back.Chamfer.Screws"
  Angle = 45
  Base = -> Fillet004 [Edge73,Edge71,Edge69,Edge42,Edge43]
  BaseFeature = -> Fillet004
  ChamferType = 0
  FlipDirection = false
  Size = 1.4
  Size2 = 1
  SupportTransform = false
  UseAllEdges = false
FEATURE [PartDesign::Body] Body  label="BodyBack"
  BaseFeature = -> Slice_child1
  Group = -> [BaseFeature,Sketch032,Pocket,Fillet,Fillet009,Fillet004,Chamfer]
  Origin = -> Origin
  Tip = -> Chamfer
FEATURE [PartDesign::Fillet] Fillet010  label="Case.Fillet.Bottom"
  Base = -> Fillet005 [Edge118,Edge99]
  BaseFeature = -> Fillet005
  Radius = 3
  SupportTransform = false
  UseAllEdges = false
  expr: Radius = <<param>>.radius_medium
FEATURE [PartDesign::Fillet] Fillet011  label="Case.Fillet.Face"
  Base = -> Fillet010 [Edge81]
  BaseFeature = -> Fillet010
  Radius = 2
  SupportTransform = false
  UseAllEdges = false
  expr: Radius = <<param>>.radius_small
FEATURE [PartDesign::Fillet] Fillet012  label="Case.Fillet.Lower"
  Base = -> Fillet011 [Edge8]
  BaseFeature = -> Fillet011
  Radius = 2
  SupportTransform = false
  UseAllEdges = false
  expr: Radius = <<param>>.radius_small
FEATURE [PartDesign::Body] Body004  label="BodyCase"
  BaseFeature = -> Slice_child0
  Group = -> [BaseFeature001,Sketch008,Sketch029,Sketch018,Sketch019,Sketch021,Sketch022,Sketch023,Sketch024,Sketch025,Sketch026,Sketch027,Sketch028,Sketch,Pocket001,Pad,Pocket002,Pocket006,Pocket005,Pocket010,SubtractiveLoft,Revolution,Pocket007,Groove,Pocket004,Fillet008,Pocket003,Fillet005,Fillet010,Fillet011,Fillet012,Sketch037]
  Origin = -> Origin005
  Tip = -> Fillet012
FEATURE [Mesh::Feature] Mesh  label="BodyBack (Meshed)"
FEATURE [Mesh::Feature] Mesh008  label="BodyCase (Meshed)"
FEATURE [Mesh::Feature] Mesh009  label="BodyFaceKSGER (Meshed)"
FEATURE [App::DocumentObjectGroup] Group  label="Mesh"
  Group = -> [Mesh006,Mesh007,Mesh,Mesh008,Mesh009]
FEATURE [PartDesign::FeatureBase] Clone
  BaseFeature = -> Body005
  Placement = pos=(0,-36.7,2.8) rot=(-1,0,0;0.349066rad)
FEATURE [PartDesign::Plane] DatumPlane
  AttachmentOffset = pos=(0,0,1.5) rot=(0,0,1;0rad)
  Length = 103.21
  MapMode = 3
  Placement = pos=(0,-38.1095,3.31303) rot=(1,0,0;1.22173rad)
  ResizeMode = 0
  Support = -> [Clone]
  Width = 102.115
  expr: .AttachmentOffset.Base.z = <<param>>.face_thickness / 2
FEATURE [Part::Part2DObjectPython] ShapeString  # Draft 2D object (typed FeaturePython)
  AttachmentOffset = pos=(4,4,0) rot=(0,0,1;0rad)
  FontFile = <path>
  MakeFace = true
  MapMode = 5
  Placement = pos=(4,-36.7415,7.0718) rot=(1,0,0;1.22173rad)
  Size = 5
  String = KSGER
  Support = -> [DatumPlane]
  Tracking = 0
FEATURE [PartDesign::Pocket] Pocket011
  BaseFeature = -> Clone
  Direction = (0,0.939693,-0.34202)
  Length = 3
  Length2 = 5
  Placement = pos=(0,-36.7,2.8) rot=(-1,0,0;0.349066rad)
  Profile = -> ShapeString
  ReferenceAxis = -> ShapeString [N_Axis]
  Reversed = true
  Type = 0
  expr: Length = <<param>>.face_thickness
FEATURE [PartDesign::Body] Body007  label="BodyFaceKSGER"
  BaseFeature = -> Body005
  Group = -> [Clone,DatumPlane,ShapeString,Pocket011]
  Origin = -> Origin009
  Tip = -> Pocket011
FEATURE [App::Part] Part
  Group = -> [Extrude,Plane002,Common,Sketch012,Loft,Slice_child1,Slice_child0,Slice,GrExplode_Slice,Sketch030,Sketch031,Group001,Spreadsheet,Body,Body004,Body005,Body007]
  Origin = -> Origin006
note: 1 file-system path scrubbed to <path> (originals preserved in the JSON sidecar)
